FCSTD DOCUMENT  (FreeCAD 1.0R)
Label: mpair
License: All rights reserved
LicenseURL: https://en.wikipedia.org/wiki/All_rights_reserved
objects: Part::Feature×225, App::Link×145, App::Part×35, PartDesign::CoordinateSystem×1, Sketcher::SketchObject×1
note: 228 computed .brp shape members not serialized (recipe doc carries the construction recipe); baked Part::Feature solids carry a one-line shape summary decoded from their .brp

FEATURE [PartDesign::CoordinateSystem] Local_CS_39ef
  AttacherType = Attacher::AttachEngine3D
  MapMode = 2
FEATURE [Part::Feature] Pcb_39ef
  shape: bbox 100 x 102 x 1.6 mm, 117 faces (baked)
FEATURE [Sketcher::SketchObject] PCB_Sketch_39ef
  ArcFitTolerance = 1e-06
  FullyConstrained = false
  MakeInternals = false
  sketch-geometry (4):
    g0: LineSegment StartX=20 StartY=-18 StartZ=0 EndX=120 EndY=-18 EndZ=0
    g1: LineSegment StartX=120 StartY=-18 StartZ=0 EndX=120 EndY=-120 EndZ=0
    g2: LineSegment StartX=120 StartY=-120 StartZ=0 EndX=20 EndY=-120 EndZ=0
    g3: LineSegment StartX=20 StartY=-120 StartZ=0 EndX=20 EndY=-18 EndZ=0
  constraints (4):
    c: Coincident(g2,g3)
    c: Coincident(g0,g3)
    c: Coincident(g1,g2)
    c: Coincident(g0,g1)
FEATURE [App::Part] Board_Geoms_39ef
  Group = -> [Pcb_39ef,PCB_Sketch_39ef]
  Origin = -> Origin
FEATURE [Part::Feature] Shape  label="R46_R_0603_1608Metric_774aaaae9ccb"
  Placement = pos=(48.7,-50.2,0) rot=(0,0,1;0rad)
  shape: bbox 1.6 x 0.8 x 0.45 mm, 26 faces (baked)
FEATURE [App::Link] R46_R_0603_1608Metric_774aaaae9ccb_ln_  label="R34_R_0603_1608Metric_f5142b1c6ad6"
  LinkPlacement = pos=(51.175,-36.55,0) rot=(0,0,1;1.5708rad)
  LinkedObject = -> Shape
  Placement = pos=(51.175,-36.55,0) rot=(0,0,1;1.5708rad)
FEATURE [Part::Feature] Shape001  label="L4_L_0805_2012Metric_8a03def62cda"
  Placement = pos=(36.31,-53.75,0) rot=(0,0,1;1.5708rad)
  shape: bbox 1.25 x 2 x 1.25 mm, 28 faces (baked)
FEATURE [Part::Feature] Shape002  label="C15_C_0603_1608Metric_07e9d6ced425"
  Placement = pos=(52.4,-28.375,0) rot=(0,0,1;1.5708rad)
  shape: bbox 0.8 x 1.6 x 0.8 mm, 28 faces (baked)
FEATURE [App::Link] R46_R_0603_1608Metric_774aaaae9ccb_ln_001  label="R17_R_0603_1608Metric_bdc7fd87b56f"
  LinkPlacement = pos=(47.1,-28.725,0) rot=(0,0,-1;1.5708rad)
  LinkedObject = -> Shape
  Placement = pos=(47.1,-28.725,0) rot=(0,0,-1;1.5708rad)
FEATURE [Part::Feature] Shape003  label="C27_CP_Elec_8x62_1d99a2359d83"
  Placement = pos=(42.6675,-54.45,0) rot=(0,0,1;0rad)
  shape: bbox 10.73 x 10.92 x 6.2 mm, 41 faces (baked)
FEATURE [App::Link] C15_C_0603_1608Metric_07e9d6ced425_ln_  label="C39_C_0603_1608Metric_8ad4aeb55371"
  LinkPlacement = pos=(41.4,-88.125,0) rot=(0,0,-1;1.5708rad)
  LinkedObject = -> Shape002
  Placement = pos=(41.4,-88.125,0) rot=(0,0,-1;1.5708rad)
FEATURE [Part::Feature] Shape004  label="L7_L_0603_1608Metric_04b4d3cc0712"
  Placement = pos=(66.8125,-31.6,0) rot=(0,0,1;0rad)
  shape: bbox 1.6 x 0.8 x 0.8 mm, 28 faces (baked)
FEATURE [Part::Feature] Part__Feature  label="DR74-2R2-R"
  shape: bbox 7.6 x 0.8 x 5.493 mm, 71 faces (baked)
FEATURE [Part::Feature] Part__Feature001  label="DR74-2R2-R001"
  shape: bbox 7.6 x 3.95 x 7.6 mm, 70 faces (baked)
FEATURE [App::Part] DR74_2R2_R  label="L13_DR74-2R2-R002_60edd9ad2b36"
  Group = -> [Part__Feature,Part__Feature001]
  Origin = -> Origin008
  Placement = pos=(81.1972,-77.9,0) rot=(1,0,0;1.5708rad)
FEATURE [App::Link] R46_R_0603_1608Metric_774aaaae9ccb_ln_002  label="R21_R_0603_1608Metric_3d0d8529494c"
  LinkPlacement = pos=(50.7,-28.425,0) rot=(0,0,-1;1.5708rad)
  LinkedObject = -> Shape
  Placement = pos=(50.7,-28.425,0) rot=(0,0,-1;1.5708rad)
FEATURE [App::Link] R46_R_0603_1608Metric_774aaaae9ccb_ln_003  label="R54_R_0603_1608Metric_98e4eba829c8"
  LinkPlacement = pos=(41.4,-91.5,0) rot=(0,0,-1;1.5708rad)
  LinkedObject = -> Shape
  Placement = pos=(41.4,-91.5,0) rot=(0,0,-1;1.5708rad)
FEATURE [Part::Feature] Shape005  label="U8_SOT_23_6_8216086f4dbc"
  Placement = pos=(78.15,-100.65,0) rot=(0,0,-1;1.5708rad)
  shape: bbox 2.9 x 2.8 x 1.55 mm, 124 faces (baked)
FEATURE [Part::Feature] Part__Feature002  label="BxB-ZR-SM4_6"
  Placement = pos=(-4.5,4e-16,-1.85) rot=(0,1,0;3.14159rad)
  shape: bbox 12 x 5 x 3.7 mm, 62 faces (baked)
FEATURE [Part::Feature] Part__Feature003  label="BxB-ZR-SM4 pins_6"
  Placement = pos=(-4.5,4e-16,-1.85) rot=(0,1,0;3.14159rad)
  shape: bbox 0.6 x 3.75 x 2.5 mm, 16 faces (baked)
FEATURE [Part::Feature] Part__Feature004  label="BxB-ZR-SM4 pins_007"
  Placement = pos=(-4.5,4e-16,-1.85) rot=(0,1,0;3.14159rad)
  shape: bbox 0.5 x 0.5 x 1.5 mm, 6 faces (baked)
FEATURE [Part::Feature] Part__Feature005  label="BxB-ZR-SM4 pins_008"
  Placement = pos=(-4.5,4e-16,-1.85) rot=(0,1,0;3.14159rad)
  shape: bbox 0.5 x 2.4 x 0.5 mm, 6 faces (baked)
FEATURE [Part::Feature] Part__Feature006  label="BxB-ZR-SM4 pins_009"
  Placement = pos=(-4.5,4e-16,-1.85) rot=(0,1,0;3.14159rad)
  shape: bbox 0.6 x 3.75 x 2.5 mm, 16 faces (baked)
FEATURE [Part::Feature] Part__Feature007  label="BxB-ZR-SM4 pins_010"
  Placement = pos=(-4.5,4e-16,-1.85) rot=(0,1,0;3.14159rad)
  shape: bbox 0.5 x 0.5 x 1.5 mm, 6 faces (baked)
FEATURE [Part::Feature] Part__Feature008  label="BxB-ZR-SM4 pins_011"
  Placement = pos=(-4.5,4e-16,-1.85) rot=(0,1,0;3.14159rad)
  shape: bbox 0.5 x 2.4 x 0.5 mm, 6 faces (baked)
FEATURE [Part::Feature] Part__Feature009  label="BxB-ZR-SM4 pins_012"
  Placement = pos=(-4.5,4e-16,-1.85) rot=(0,1,0;3.14159rad)
  shape: bbox 0.5 x 0.5 x 1.5 mm, 6 faces (baked)
FEATURE [Part::Feature] Part__Feature010  label="BxB-ZR-SM4 pins_013"
  Placement = pos=(-4.5,4e-16,-1.85) rot=(0,1,0;3.14159rad)
  shape: bbox 0.5 x 2.4 x 0.5 mm, 6 faces (baked)
FEATURE [Part::Feature] Part__Feature011  label="BxB-ZR-SM4 pins_014"
  Placement = pos=(-4.5,4e-16,-1.85) rot=(0,1,0;3.14159rad)
  shape: bbox 0.5 x 0.5 x 1.5 mm, 6 faces (baked)
FEATURE [Part::Feature] Part__Feature012  label="BxB-ZR-SM4 pins_015"
  Placement = pos=(-4.5,4e-16,-1.85) rot=(0,1,0;3.14159rad)
  shape: bbox 0.5 x 0.5 x 1.5 mm, 6 faces (baked)
FEATURE [Part::Feature] Part__Feature013  label="BxB-ZR-SM4 pins_016"
  Placement = pos=(-4.5,4e-16,-1.85) rot=(0,1,0;3.14159rad)
  shape: bbox 0.5 x 0.5 x 1.5 mm, 6 faces (baked)
FEATURE [Part::Feature] Part__Feature014  label="BxB-ZR-SM4 pins_017"
  Placement = pos=(-4.5,4e-16,-1.85) rot=(0,1,0;3.14159rad)
  shape: bbox 0.5 x 2.4 x 0.5 mm, 6 faces (baked)
FEATURE [Part::Feature] Part__Feature015  label="BxB-ZR-SM4 pins_018"
  Placement = pos=(-4.5,4e-16,-1.85) rot=(0,1,0;3.14159rad)
  shape: bbox 0.5 x 2.4 x 0.5 mm, 6 faces (baked)
FEATURE [Part::Feature] Part__Feature016  label="BxB-ZR-SM4 pins_019"
  Placement = pos=(-4.5,4e-16,-1.85) rot=(0,1,0;3.14159rad)
  shape: bbox 0.5 x 2.4 x 0.5 mm, 6 faces (baked)
FEATURE [App::Part] BxB_ZR_SM4_pins_6  label="BxB-ZR-SM4 pins_020"
  Group = -> [Part__Feature003,Part__Feature004,Part__Feature005,Part__Feature006,Part__Feature007,Part__Feature008,Part__Feature009,Part__Feature010,Part__Feature011,Part__Feature012,Part__Feature013,Part__Feature014,Part__Feature015,Part__Feature016]
  Origin = -> Origin009
FEATURE [App::Part] B6B_ZR_SM4_TF  label="J5_B6B-ZR-SM4-TF_bfa23934778d"
  Group = -> [Part__Feature002,BxB_ZR_SM4_pins_6]
  Origin = -> Origin010
  Placement = pos=(91.3,-112.4,0) rot=(0.57735,0.57735,0.57735;2.0944rad)
FEATURE [Part::Feature] Shape006  label="J9_Molex_AE_6410_03A_8847f52549e1"
  Placement = pos=(100.1,-117.7,0) rot=(0,0,1;1.5708rad)
  shape: bbox 5.8 x 7.62 x 15.26 mm, 91 faces (baked)
FEATURE [App::Link] R46_R_0603_1608Metric_774aaaae9ccb_ln_004  label="R7_R_0603_1608Metric_40a0c56f9955"
  LinkPlacement = pos=(103.65,-104.875,0) rot=(0,0,1;0rad)
  LinkedObject = -> Shape
  Placement = pos=(103.65,-104.875,0) rot=(0,0,1;0rad)
FEATURE [Part::Feature] Part__Feature017  label="part"
  shape: bbox 0.2197 x 0.2197 x 0.002 mm, 3 faces (baked)
FEATURE [Part::Feature] Part__Feature018  label="part001"
  shape: bbox 4.399 x 2.695 x 2.39 mm, 14 faces (baked)
FEATURE [Part::Feature] Part__Feature019  label="part002"
  shape: bbox 1.45 x 0.5096 x 1.323 mm, 14 faces (baked)
FEATURE [Part::Feature] Part__Feature020  label="part003"
  shape: bbox 1.45 x 0.5096 x 1.323 mm, 14 faces (baked)
FEATURE [Part::Feature] Part__Feature021  label="part004"
  shape: bbox 1.45 x 0.5096 x 1.323 mm, 14 faces (baked)
FEATURE [Part::Feature] Part__Feature022  label="part005"
  shape: bbox 1.45 x 0.5096 x 1.323 mm, 14 faces (baked)
FEATURE [App::Part] part  label="U6_part006_fb86ca2d76d7"
  Group = -> [Part__Feature017,Part__Feature018,Part__Feature019,Part__Feature020,Part__Feature021,Part__Feature022]
  Origin = -> Origin011
  Placement = pos=(40.2,-78.3,0) rot=(0,0,1;1.5708rad)
FEATURE [Part::Feature] Shape007  label="C34_C_1812_4532Metric_c9e1e99fbcf3"
  Placement = pos=(44.2,-78.3,0) rot=(0,0,-1;1.5708rad)
  shape: bbox 3.2 x 4.5 x 2.5 mm, 28 faces (baked)
FEATURE [App::Link] R46_R_0603_1608Metric_774aaaae9ccb_ln_005  label="R13_R_0603_1608Metric_f67d6ac71e9b"
  LinkPlacement = pos=(47.5,-24.5,0) rot=(0,0,-1;1.5708rad)
  LinkedObject = -> Shape
  Placement = pos=(47.5,-24.5,0) rot=(0,0,-1;1.5708rad)
FEATURE [App::Link] R46_R_0603_1608Metric_774aaaae9ccb_ln_006  label="R12_R_0603_1608Metric_d3075d49b59f"
  LinkPlacement = pos=(28.225,-19.95,0) rot=(0,0,1;0rad)
  LinkedObject = -> Shape
  Placement = pos=(28.225,-19.95,0) rot=(0,0,1;0rad)
FEATURE [Part::Feature] Shape008  label="C42_CP_Elec_8x10_2bb510fd45c5"
  Placement = pos=(73.1,-112.4,0) rot=(0,0,-1;1.5708rad)
  shape: bbox 10.92 x 10.73 x 10 mm, 41 faces (baked)
FEATURE [App::Link] R46_R_0603_1608Metric_774aaaae9ccb_ln_007  label="R3_R_0603_1608Metric_7ba40911dab3"
  LinkPlacement = pos=(110.45,-103.7,0) rot=(0,0,-1;1.5708rad)
  LinkedObject = -> Shape
  Placement = pos=(110.45,-103.7,0) rot=(0,0,-1;1.5708rad)
FEATURE [App::Link] R46_R_0603_1608Metric_774aaaae9ccb_ln_008  label="R64_R_0603_1608Metric_9be8635e4ac9"
  LinkPlacement = pos=(111.6,-63.5,0) rot=(0,0,-1;1.5708rad)
  LinkedObject = -> Shape
  Placement = pos=(111.6,-63.5,0) rot=(0,0,-1;1.5708rad)
FEATURE [Part::Feature] Part__Feature023  label="BarrelJack_CUI_PJ-063AH_Horizontal"
  shape: bbox 9.8 x 8.6 x 11.9 mm, 54 faces (baked)
FEATURE [Part::Feature] Part__Feature024  label="BarrelJack_CUI_PJ-063AH_Horizontal001"
  shape: bbox 10 x 13 x 12 mm, 42 faces (baked)
FEATURE [App::Part] BarrelJack_CUI_PJ_063AH_Horizontal  label="J1_BarrelJack_CUI_PJ-063AH_Horizontal002_36d1827e98da"
  Group = -> [Part__Feature023,Part__Feature024]
  Origin = -> Origin012
  Placement = pos=(32.4,-112.4,0) rot=(0,0,-1;1.5708rad)
FEATURE [Part::Feature] Shape009  label="Q8_SC_59_2bd4244db7e1"
  Placement = pos=(114.8,-108.75,0) rot=(0,0,1;3.14159rad)
  shape: bbox 2.8 x 3 x 1.3 mm, 76 faces (baked)
FEATURE [Part::Feature] Shape010  label="C25_C_0805_2012Metric_74a1367a9602"
  Placement = pos=(58.2,-56.55,0) rot=(0,0,1;1.5708rad)
  shape: bbox 1.25 x 2 x 1.25 mm, 28 faces (baked)
FEATURE [App::Link] R46_R_0603_1608Metric_774aaaae9ccb_ln_009  label="R70_R_0603_1608Metric_297dd1acad90"
  LinkPlacement = pos=(81.7,-64.1,0) rot=(0,0,-1;1.5708rad)
  LinkedObject = -> Shape
  Placement = pos=(81.7,-64.1,0) rot=(0,0,-1;1.5708rad)
FEATURE [App::Link] C15_C_0603_1608Metric_07e9d6ced425_ln_001  label="C23_C_0603_1608Metric_376995170c63"
  LinkPlacement = pos=(69.925,-31.6,0) rot=(0,0,1;0rad)
  LinkedObject = -> Shape002
  Placement = pos=(69.925,-31.6,0) rot=(0,0,1;0rad)
FEATURE [App::Link] L4_L_0805_2012Metric_8a03def62cda_ln_  label="L5_L_0805_2012Metric_fc17c2d6df8f"
  LinkPlacement = pos=(98.65,-103.838,0) rot=(0,0,-1;1.5708rad)
  LinkedObject = -> Shape001
  Placement = pos=(98.65,-103.838,0) rot=(0,0,-1;1.5708rad)
FEATURE [App::Link] C15_C_0603_1608Metric_07e9d6ced425_ln_002  label="C29_C_0603_1608Metric_f624abb60192"
  LinkPlacement = pos=(52,-53.8,0) rot=(0,0,1;0rad)
  LinkedObject = -> Shape002
  Placement = pos=(52,-53.8,0) rot=(0,0,1;0rad)
FEATURE [Part::Feature] Shape011  label="R51_R_0805_2012Metric_3a37762b02a9"
  Placement = pos=(66.95,-97.15,0) rot=(0,0,-1;1.5708rad)
  shape: bbox 1.2 x 2 x 0.45 mm, 26 faces (baked)
FEATURE [App::Link] C15_C_0603_1608Metric_07e9d6ced425_ln_003  label="C5_C_0603_1608Metric_a1c9e7e04d42"
  LinkPlacement = pos=(36.31,-48.75,0) rot=(0,0,-1;1.5708rad)
  LinkedObject = -> Shape002
  Placement = pos=(36.31,-48.75,0) rot=(0,0,-1;1.5708rad)
FEATURE [App::Link] R46_R_0603_1608Metric_774aaaae9ccb_ln_010  label="R53_R_0603_1608Metric_e281e5424af1"
  LinkPlacement = pos=(39.5,-88.1,0) rot=(0,0,1;1.5708rad)
  LinkedObject = -> Shape
  Placement = pos=(39.5,-88.1,0) rot=(0,0,1;1.5708rad)
FEATURE [App::Link] R46_R_0603_1608Metric_774aaaae9ccb_ln_011  label="R60_R_0603_1608Metric_86f9834c2b51"
  LinkPlacement = pos=(115.4,-63.5,0) rot=(0,0,-1;1.5708rad)
  LinkedObject = -> Shape
  Placement = pos=(115.4,-63.5,0) rot=(0,0,-1;1.5708rad)
FEATURE [Part::Feature] Shape012  label="D6_D_SMB_3d57ee7d56c4"
  Placement = pos=(60.2,-43.3,0) rot=(0,0,-1;1.5708rad)
  shape: bbox 3.55 x 5.3 x 2.15 mm, 41 faces (baked)
FEATURE [App::Link] Q8_SC_59_2bd4244db7e1_ln_  label="D14_SC_59_adce9ebe72b1"
  LinkPlacement = pos=(62.75,-97.15,0) rot=(0,0,1;0rad)
  LinkedObject = -> Shape009
  Placement = pos=(62.75,-97.15,0) rot=(0,0,1;0rad)
FEATURE [App::Link] C15_C_0603_1608Metric_07e9d6ced425_ln_004  label="C49_C_0603_1608Metric_8a9601e40898"
  LinkPlacement = pos=(81.9,-84.4,0) rot=(0,0,-1;1.5708rad)
  LinkedObject = -> Shape002
  Placement = pos=(81.9,-84.4,0) rot=(0,0,-1;1.5708rad)
FEATURE [App::Link] Q8_SC_59_2bd4244db7e1_ln_001  label="D10_SC_59_9d504f3714de"
  LinkPlacement = pos=(57.1,-97.15,0) rot=(0,0,1;3.14159rad)
  LinkedObject = -> Shape009
  Placement = pos=(57.1,-97.15,0) rot=(0,0,1;3.14159rad)
FEATURE [Part::Feature] Shape013  label="D3_D_0603_7257a63e26b1"
  Placement = pos=(54.2,-23.2625,0) rot=(0,0,-1;1.5708rad)
  shape: bbox 0.87 x 1.6 x 0.66 mm, 39 faces (baked)
FEATURE [Part::Feature] Shape014  label="C7_C_1210_3225Metric_ef0ee58cb2a3"
  Placement = pos=(99.45,-97.075,0) rot=(0,0,1;1.5708rad)
  shape: bbox 2.5 x 3.2 x 2.5 mm, 28 faces (baked)
FEATURE [Part::Feature] Shape015  label="D16_D_SOD_123_001db0ef50de"
  Placement = pos=(108.8,-107.1,0) rot=(0,0,1;0rad)
  shape: bbox 3.8 x 1.6 x 1.25 mm, 67 faces (baked)
FEATURE [Part::Feature] Part__Feature025  label="part006"
  shape: bbox 0.1295 x 0.1295 x 0.003 mm, 3 faces (baked)
FEATURE [Part::Feature] Part__Feature026  label="part007"
  shape: bbox 2.59 x 3.404 x 2.133 mm, 6 faces (baked)
FEATURE [Part::Feature] Part__Feature027  label="part008"
  shape: bbox 0.829 x 0.533 x 0.381 mm, 8 faces (baked)
FEATURE [Part::Feature] Part__Feature028  label="part009"
  shape: bbox 0.829 x 0.533 x 0.381 mm, 8 faces (baked)
FEATURE [Part::Feature] Part__Feature029  label="part010"
  shape: bbox 0.829 x 0.533 x 0.381 mm, 8 faces (baked)
FEATURE [Part::Feature] Part__Feature030  label="part011"
  shape: bbox 0.829 x 0.533 x 0.381 mm, 8 faces (baked)
FEATURE [App::Part] part001  label="L8_part012_f921aaf74477"
  Group = -> [Part__Feature025,Part__Feature026,Part__Feature027,Part__Feature028,Part__Feature029,Part__Feature030]
  Origin = -> Origin013
  Placement = pos=(45.627,-36.5,0) rot=(0,0,1;1.5708rad)
FEATURE [Part::Feature] Shape016  label="RN1_R_Array_Concave_4x0603_af55f0de138e"
  Placement = pos=(51.55,-24.85,0) rot=(0,0,1;0rad)
  shape: bbox 1.6 x 3.2 x 0.6 mm, 140 faces (baked)
FEATURE [App::Link] C7_C_1210_3225Metric_ef0ee58cb2a3_ln_  label="C41_C_1210_3225Metric_231fadff6d53"
  LinkPlacement = pos=(66.6,-109.15,0) rot=(0,0,1;1.5708rad)
  LinkedObject = -> Shape014
  Placement = pos=(66.6,-109.15,0) rot=(0,0,1;1.5708rad)
FEATURE [Part::Feature] Part__Feature031  label="part012"
  shape: bbox 0.2299 x 0.2299 x 0.003 mm, 3 faces (baked)
FEATURE [Part::Feature] Part__Feature032  label="part013"
  shape: bbox 4.602 x 3.915 x 3 mm, 14 faces (baked)
FEATURE [Part::Feature] Part__Feature033  label="part014"
  shape: bbox 1.296 x 0.5094 x 1.627 mm, 14 faces (baked)
FEATURE [Part::Feature] Part__Feature034  label="part015"
  shape: bbox 1.296 x 0.5094 x 1.627 mm, 14 faces (baked)
FEATURE [Part::Feature] Part__Feature035  label="part016"
  shape: bbox 1.296 x 0.5094 x 1.627 mm, 14 faces (baked)
FEATURE [Part::Feature] Part__Feature036  label="part017"
  shape: bbox 1.296 x 0.5094 x 1.627 mm, 14 faces (baked)
FEATURE [App::Part] part002  label="U7_part018_2105863d2e2c"
  Group = -> [Part__Feature031,Part__Feature032,Part__Feature033,Part__Feature034,Part__Feature035,Part__Feature036]
  Origin = -> Origin014
  Placement = pos=(74.5,-70.3,0) rot=(0,0,1;0rad)
FEATURE [Part::Feature] Shape017  label="C26_C_1206_3216Metric_2a08b5551de6"
  Placement = pos=(57.5,-65.025,0) rot=(0,0,1;1.5708rad)
  shape: bbox 1.6 x 3.2 x 1.6 mm, 28 faces (baked)
FEATURE [App::Link] R46_R_0603_1608Metric_774aaaae9ccb_ln_012  label="R37_R_0603_1608Metric_6502443f79bd"
  LinkPlacement = pos=(60.65,-36.55,0) rot=(0,0,1;1.5708rad)
  LinkedObject = -> Shape
  Placement = pos=(60.65,-36.55,0) rot=(0,0,1;1.5708rad)
FEATURE [App::Link] C15_C_0603_1608Metric_07e9d6ced425_ln_005  label="C4_C_0603_1608Metric_b8aa947e1a63"
  LinkPlacement = pos=(36.2,-112.4,0) rot=(0,0,-1;1.5708rad)
  LinkedObject = -> Shape002
  Placement = pos=(36.2,-112.4,0) rot=(0,0,-1;1.5708rad)
FEATURE [App::Link] C7_C_1210_3225Metric_ef0ee58cb2a3_ln_001  label="C40_C_1210_3225Metric_2fc55fe14432"
  LinkPlacement = pos=(66.6,-115.675,0) rot=(0,0,-1;1.5708rad)
  LinkedObject = -> Shape014
  Placement = pos=(66.6,-115.675,0) rot=(0,0,-1;1.5708rad)
FEATURE [App::Link] R46_R_0603_1608Metric_774aaaae9ccb_ln_013  label="R61_R_0603_1608Metric_1d752b88a0c3"
  LinkPlacement = pos=(107.8,-63.5,0) rot=(0,0,-1;1.5708rad)
  LinkedObject = -> Shape
  Placement = pos=(107.8,-63.5,0) rot=(0,0,-1;1.5708rad)
FEATURE [Part::Feature] Shape018  label="D1_D_SMA_e719b518da9d"
  Placement = pos=(40.36,-45.45,0) rot=(0,0,-1;1.5708rad)
  shape: bbox 2.7 x 5 x 2.22 mm, 41 faces (baked)
FEATURE [App::Link] R46_R_0603_1608Metric_774aaaae9ccb_ln_014  label="R20_R_0603_1608Metric_5ae41c8f7d63"
  LinkPlacement = pos=(44.675,-20.35,0) rot=(0,0,1;0rad)
  LinkedObject = -> Shape
  Placement = pos=(44.675,-20.35,0) rot=(0,0,1;0rad)
FEATURE [Part::Feature] Part__Feature037  label="SRR1208"
  shape: bbox 12.7 x 2.2 x 12.7 mm, 30 faces (baked)
FEATURE [Part::Feature] Part__Feature038  label="SRR1209"
  shape: bbox 12.7 x 7.2 x 12.7 mm, 40 faces (baked)
FEATURE [App::Part] SRR1208  label="L11_SRR1210_1625587d1eb0"
  Group = -> [Part__Feature037,Part__Feature038]
  Origin = -> Origin015
  Placement = pos=(48.4,-112.25,0.2) rot=(1,0,0;1.5708rad)
FEATURE [App::Link] L4_L_0805_2012Metric_8a03def62cda_ln_001  label="L2_L_0805_2012Metric_cfc35715fd5a"
  LinkPlacement = pos=(36.2,-117.4,0) rot=(0,0,1;1.5708rad)
  LinkedObject = -> Shape001
  Placement = pos=(36.2,-117.4,0) rot=(0,0,1;1.5708rad)
FEATURE [App::Link] C15_C_0603_1608Metric_07e9d6ced425_ln_006  label="C17_C_0603_1608Metric_233d63a9970e"
  LinkPlacement = pos=(60.6625,-33.375,0) rot=(0,0,1;1.5708rad)
  LinkedObject = -> Shape002
  Placement = pos=(60.6625,-33.375,0) rot=(0,0,1;1.5708rad)
FEATURE [App::Link] D16_D_SOD_123_001db0ef50de_ln_  label="D13_D_SOD_123_f0bbc3cf7802"
  LinkPlacement = pos=(48.8,-94.6,0) rot=(0,0,1;1.5708rad)
  LinkedObject = -> Shape015
  Placement = pos=(48.8,-94.6,0) rot=(0,0,1;1.5708rad)
FEATURE [App::Link] C15_C_0603_1608Metric_07e9d6ced425_ln_007  label="C8_C_0603_1608Metric_3d25220c7f24"
  LinkPlacement = pos=(100.55,-104.1,0) rot=(0,0,1;1.5708rad)
  LinkedObject = -> Shape002
  Placement = pos=(100.55,-104.1,0) rot=(0,0,1;1.5708rad)
FEATURE [App::Link] R46_R_0603_1608Metric_774aaaae9ccb_ln_015  label="R14_R_0603_1608Metric_b8c0ad13ef43"
  LinkPlacement = pos=(43.7,-24.475,0) rot=(0,0,-1;1.5708rad)
  LinkedObject = -> Shape
  Placement = pos=(43.7,-24.475,0) rot=(0,0,-1;1.5708rad)
FEATURE [App::Link] U8_SOT_23_6_8216086f4dbc_ln_  label="U9_SOT_23_6_7fa43c93b1dc"
  LinkPlacement = pos=(78.15,-85.1625,0) rot=(0,0,-1;1.5708rad)
  LinkedObject = -> Shape005
  Placement = pos=(78.15,-85.1625,0) rot=(0,0,-1;1.5708rad)
FEATURE [App::Link] C7_C_1210_3225Metric_ef0ee58cb2a3_ln_002  label="C44_C_1210_3225Metric_7e9aa11df215"
  LinkPlacement = pos=(74.2,-95.2,0) rot=(0,0,-1;1.5708rad)
  LinkedObject = -> Shape014
  Placement = pos=(74.2,-95.2,0) rot=(0,0,-1;1.5708rad)
FEATURE [App::Link] R46_R_0603_1608Metric_774aaaae9ccb_ln_016  label="R56_R_0603_1608Metric_0e1817b85848"
  LinkPlacement = pos=(79.625,-103.6,0) rot=(0,0,1;3.14159rad)
  LinkedObject = -> Shape
  Placement = pos=(79.625,-103.6,0) rot=(0,0,1;3.14159rad)
FEATURE [App::Link] Q8_SC_59_2bd4244db7e1_ln_002  label="D11_SC_59_5ee113a929a4"
  LinkPlacement = pos=(46.8,-84.6,0) rot=(0,0,1;0rad)
  LinkedObject = -> Shape009
  Placement = pos=(46.8,-84.6,0) rot=(0,0,1;0rad)
FEATURE [App::Link] C25_C_0805_2012Metric_74a1367a9602_ln_  label="C36_C_0805_2012Metric_0ec6a73c6179"
  LinkPlacement = pos=(43.6,-84.6,0) rot=(0,0,1;1.5708rad)
  LinkedObject = -> Shape010
  Placement = pos=(43.6,-84.6,0) rot=(0,0,1;1.5708rad)
FEATURE [App::Link] Q8_SC_59_2bd4244db7e1_ln_003  label="D12_SC_59_1be8da5ed14b"
  LinkPlacement = pos=(46.4,-88.8,0) rot=(0,0,1;0rad)
  LinkedObject = -> Shape009
  Placement = pos=(46.4,-88.8,0) rot=(0,0,1;0rad)
FEATURE [App::Link] C15_C_0603_1608Metric_07e9d6ced425_ln_008  label="C37_C_0603_1608Metric_7e360995dad7"
  LinkPlacement = pos=(43.3,-88.1,0) rot=(0,0,-1;1.5708rad)
  LinkedObject = -> Shape002
  Placement = pos=(43.3,-88.1,0) rot=(0,0,-1;1.5708rad)
FEATURE [App::Link] C15_C_0603_1608Metric_07e9d6ced425_ln_009  label="C22_C_0603_1608Metric_4ce7b6444197"
  LinkPlacement = pos=(55.8,-20.9,0) rot=(0,0,-1;1.5708rad)
  LinkedObject = -> Shape002
  Placement = pos=(55.8,-20.9,0) rot=(0,0,-1;1.5708rad)
FEATURE [App::Link] C15_C_0603_1608Metric_07e9d6ced425_ln_010  label="C10_C_0603_1608Metric_b3e33615cffe"
  LinkPlacement = pos=(48.9,-28.675,0) rot=(0,0,1;1.5708rad)
  LinkedObject = -> Shape002
  Placement = pos=(48.9,-28.675,0) rot=(0,0,1;1.5708rad)
FEATURE [Part::Feature] Shape019  label="Q1_SOT_363_SC_70_6_98748a45afd2"
  Placement = pos=(104.9,-96.225,0) rot=(0,0,1;3.14159rad)
  shape: bbox 2 x 2 x 1.05 mm, 118 faces (baked)
FEATURE [App::Link] R46_R_0603_1608Metric_774aaaae9ccb_ln_017  label="R43_R_0603_1608Metric_f50d1f320f3e"
  LinkPlacement = pos=(52,-55.6,0) rot=(0,0,1;0rad)
  LinkedObject = -> Shape
  Placement = pos=(52,-55.6,0) rot=(0,0,1;0rad)
FEATURE [App::Link] L13_DR74_2R2_R002_60edd9ad2b36_ln_  label="L12_DR74-2R2-R002_3baf6c89d8cf"
  LinkPlacement = pos=(81.2,-93.4,0) rot=(1,0,0;1.5708rad)
  LinkedObject = -> DR74_2R2_R
  Placement = pos=(81.2,-93.4,0) rot=(1,0,0;1.5708rad)
FEATURE [App::Link] Q8_SC_59_2bd4244db7e1_ln_004  label="D7_SC_59_690d85af358d"
  LinkPlacement = pos=(58.2,-60.375,0) rot=(0,0,1;0rad)
  LinkedObject = -> Shape009
  Placement = pos=(58.2,-60.375,0) rot=(0,0,1;0rad)
FEATURE [App::Link] R46_R_0603_1608Metric_774aaaae9ccb_ln_018  label="R58_R_0603_1608Metric_e315c32501a6"
  LinkPlacement = pos=(79.625,-88.1,0) rot=(0,0,1;3.14159rad)
  LinkedObject = -> Shape
  Placement = pos=(79.625,-88.1,0) rot=(0,0,1;3.14159rad)
FEATURE [App::Link] R46_R_0603_1608Metric_774aaaae9ccb_ln_019  label="R67_R_0603_1608Metric_de1c96668fdd"
  LinkPlacement = pos=(95.875,-75.7,0) rot=(0,0,1;0rad)
  LinkedObject = -> Shape
  Placement = pos=(95.875,-75.7,0) rot=(0,0,1;0rad)
FEATURE [App::Link] D3_D_0603_7257a63e26b1_ln_  label="D4_D_0603_679e1ba17305"
  LinkPlacement = pos=(54.2,-26.4375,0) rot=(0,0,1;1.5708rad)
  LinkedObject = -> Shape013
  Placement = pos=(54.2,-26.4375,0) rot=(0,0,1;1.5708rad)
FEATURE [Part::Feature] Part__Feature039  label="BxB-ZR-SM4_5"
  Placement = pos=(-5.25,4e-16,-1.85) rot=(0,1,0;3.14159rad)
  shape: bbox 10.5 x 5 x 3.7 mm, 62 faces (baked)
FEATURE [Part::Feature] Part__Feature040  label="BxB-ZR-SM4 pins_5"
  Placement = pos=(-5.25,4e-16,-1.85) rot=(0,1,0;3.14159rad)
  shape: bbox 0.6 x 3.75 x 2.5 mm, 16 faces (baked)
FEATURE [Part::Feature] Part__Feature041  label="BxB-ZR-SM4 pins_021"
  Placement = pos=(-5.25,4e-16,-1.85) rot=(0,1,0;3.14159rad)
  shape: bbox 0.5 x 0.5 x 1.5 mm, 6 faces (baked)
FEATURE [Part::Feature] Part__Feature042  label="BxB-ZR-SM4 pins_022"
  Placement = pos=(-5.25,4e-16,-1.85) rot=(0,1,0;3.14159rad)
  shape: bbox 0.5 x 2.4 x 0.5 mm, 6 faces (baked)
FEATURE [Part::Feature] Part__Feature043  label="BxB-ZR-SM4 pins_023"
  Placement = pos=(-5.25,4e-16,-1.85) rot=(0,1,0;3.14159rad)
  shape: bbox 0.6 x 3.75 x 2.5 mm, 16 faces (baked)
FEATURE [Part::Feature] Part__Feature044  label="BxB-ZR-SM4 pins_024"
  Placement = pos=(-5.25,4e-16,-1.85) rot=(0,1,0;3.14159rad)
  shape: bbox 0.5 x 0.5 x 1.5 mm, 6 faces (baked)
FEATURE [Part::Feature] Part__Feature045  label="BxB-ZR-SM4 pins_025"
  Placement = pos=(-5.25,4e-16,-1.85) rot=(0,1,0;3.14159rad)
  shape: bbox 0.5 x 2.4 x 0.5 mm, 6 faces (baked)
FEATURE [Part::Feature] Part__Feature046  label="BxB-ZR-SM4 pins_026"
  Placement = pos=(-5.25,4e-16,-1.85) rot=(0,1,0;3.14159rad)
  shape: bbox 0.5 x 0.5 x 1.5 mm, 6 faces (baked)
FEATURE [Part::Feature] Part__Feature047  label="BxB-ZR-SM4 pins_027"
  Placement = pos=(-5.25,4e-16,-1.85) rot=(0,1,0;3.14159rad)
  shape: bbox 0.5 x 2.4 x 0.5 mm, 6 faces (baked)
FEATURE [Part::Feature] Part__Feature048  label="BxB-ZR-SM4 pins_028"
  Placement = pos=(-5.25,4e-16,-1.85) rot=(0,1,0;3.14159rad)
  shape: bbox 0.5 x 0.5 x 1.5 mm, 6 faces (baked)
FEATURE [Part::Feature] Part__Feature049  label="BxB-ZR-SM4 pins_029"
  Placement = pos=(-5.25,4e-16,-1.85) rot=(0,1,0;3.14159rad)
  shape: bbox 0.5 x 0.5 x 1.5 mm, 6 faces (baked)
FEATURE [Part::Feature] Part__Feature050  label="BxB-ZR-SM4 pins_030"
  Placement = pos=(-5.25,4e-16,-1.85) rot=(0,1,0;3.14159rad)
  shape: bbox 0.5 x 2.4 x 0.5 mm, 6 faces (baked)
FEATURE [Part::Feature] Part__Feature051  label="BxB-ZR-SM4 pins_031"
  Placement = pos=(-5.25,4e-16,-1.85) rot=(0,1,0;3.14159rad)
  shape: bbox 0.5 x 2.4 x 0.5 mm, 6 faces (baked)
FEATURE [App::Part] BxB_ZR_SM4_pins_5  label="BxB-ZR-SM4 pins_032"
  Group = -> [Part__Feature040,Part__Feature041,Part__Feature042,Part__Feature043,Part__Feature044,Part__Feature045,Part__Feature046,Part__Feature047,Part__Feature048,Part__Feature049,Part__Feature050,Part__Feature051]
  Origin = -> Origin016
FEATURE [App::Part] B5B_ZR_SM4_TF  label="J6_B5B-ZR-SM4-TF_078686d8772e"
  Group = -> [Part__Feature039,BxB_ZR_SM4_pins_5]
  Origin = -> Origin017
  Placement = pos=(98.2,-63.9,0) rot=(1,0,0;1.5708rad)
FEATURE [App::Link] R46_R_0603_1608Metric_774aaaae9ccb_ln_020  label="R44_R_0603_1608Metric_4ad3b6abe00a"
  LinkPlacement = pos=(49.4,-56.35,0) rot=(0,0,1;1.5708rad)
  LinkedObject = -> Shape
  Placement = pos=(49.4,-56.35,0) rot=(0,0,1;1.5708rad)
FEATURE [App::Link] C25_C_0805_2012Metric_74a1367a9602_ln_001  label="C24_C_0805_2012Metric_f408f941c3c0"
  LinkPlacement = pos=(49.15,-36.55,0) rot=(0,0,1;1.5708rad)
  LinkedObject = -> Shape010
  Placement = pos=(49.15,-36.55,0) rot=(0,0,1;1.5708rad)
FEATURE [App::Link] R46_R_0603_1608Metric_774aaaae9ccb_ln_021  label="R38_R_0603_1608Metric_163acdffd42d"
  LinkPlacement = pos=(62.575,-36.55,0) rot=(0,0,-1;1.5708rad)
  LinkedObject = -> Shape
  Placement = pos=(62.575,-36.55,0) rot=(0,0,-1;1.5708rad)
FEATURE [App::Link] C7_C_1210_3225Metric_ef0ee58cb2a3_ln_003  label="C53_C_1210_3225Metric_84c545a4b120"
  LinkPlacement = pos=(88.2,-84.9,0) rot=(0,0,-1;1.5708rad)
  LinkedObject = -> Shape014
  Placement = pos=(88.2,-84.9,0) rot=(0,0,-1;1.5708rad)
FEATURE [App::Link] R46_R_0603_1608Metric_774aaaae9ccb_ln_022  label="R9_R_0603_1608Metric_296df60f6211"
  LinkPlacement = pos=(107.95,-101.325,0) rot=(0,0,1;1.5708rad)
  LinkedObject = -> Shape
  Placement = pos=(107.95,-101.325,0) rot=(0,0,1;1.5708rad)
FEATURE [App::Link] D6_D_SMB_3d57ee7d56c4_ln_  label="D5_D_SMB_7e141658368b"
  LinkPlacement = pos=(45.6,-45.6,0) rot=(0,0,-1;1.5708rad)
  LinkedObject = -> Shape012
  Placement = pos=(45.6,-45.6,0) rot=(0,0,-1;1.5708rad)
FEATURE [Part::Feature] Part__Feature052  label="pines"
  Placement = pos=(0,0,0) rot=(1,0,0;1.5708rad)
  shape: bbox 9 x 1 x 0.8602 mm, 18 faces (baked)
FEATURE [Part::Feature] Part__Feature053  label="cuerpo"
  Placement = pos=(-3,-1.75,0) rot=(0,0,1;0rad)
  shape: bbox 6 x 3.5 x 1.8 mm, 43 faces (baked)
FEATURE [Part::Feature] Part__Feature054  label="boton"
  Placement = pos=(-0.9,-0.63,0) rot=(0,0,1;0rad)
  shape: bbox 1.8 x 1.25 x 2 mm, 18 faces (baked)
FEATURE [App::Part] ASSEMBLY  label="SW1_ASSEMBLY_b6ed21c688b7"
  Group = -> [Part__Feature052,Part__Feature053,Part__Feature054]
  Origin = -> Origin018
  Placement = pos=(110.79,-67.3,0) rot=(0,0,1;0rad)
FEATURE [Part::Feature] Shape020  label="T1_PA4065NL_3af35f8743a4"
  Placement = pos=(59.5,-78.275,-0.1) rot=(0,0,1;1.5708rad)
  shape: bbox 13.11 x 17.06 x 12.3 mm, 343 faces (baked)
FEATURE [App::Link] R46_R_0603_1608Metric_774aaaae9ccb_ln_023  label="R52_R_0603_1608Metric_9e8095a25d8f"
  LinkPlacement = pos=(43.3,-91.5,0) rot=(0,0,-1;1.5708rad)
  LinkedObject = -> Shape
  Placement = pos=(43.3,-91.5,0) rot=(0,0,-1;1.5708rad)
FEATURE [App::Link] J1_BarrelJack_CUI_PJ_063AH_Horizontal002_36d1827e98da_ln_  label="J2_BarrelJack_CUI_PJ-063AH_Horizontal002_65223e44f8ae"
  LinkPlacement = pos=(32.51,-48.75,0) rot=(0,0,-1;1.5708rad)
  LinkedObject = -> BarrelJack_CUI_PJ_063AH_Horizontal
  Placement = pos=(32.51,-48.75,0) rot=(0,0,-1;1.5708rad)
FEATURE [App::Link] R46_R_0603_1608Metric_774aaaae9ccb_ln_024  label="R57_R_0603_1608Metric_7448bebd62c0"
  LinkPlacement = pos=(76.4,-103.6,0) rot=(0,0,1;3.14159rad)
  LinkedObject = -> Shape
  Placement = pos=(76.4,-103.6,0) rot=(0,0,1;3.14159rad)
FEATURE [App::Link] D1_D_SMA_e719b518da9d_ln_  label="D2_D_SMA_857ed7a0b165"
  LinkPlacement = pos=(39.5,-110.45,0) rot=(0,0,1;1.5708rad)
  LinkedObject = -> Shape018
  Placement = pos=(39.5,-110.45,0) rot=(0,0,1;1.5708rad)
FEATURE [App::Link] C15_C_0603_1608Metric_07e9d6ced425_ln_011  label="C30_C_0603_1608Metric_dd2b13620af9"
  LinkPlacement = pos=(52,-52,0) rot=(0,0,1;0rad)
  LinkedObject = -> Shape002
  Placement = pos=(52,-52,0) rot=(0,0,1;0rad)
FEATURE [App::Link] C15_C_0603_1608Metric_07e9d6ced425_ln_012  label="C38_C_0603_1608Metric_454104598dfe"
  LinkPlacement = pos=(69.7,-103.9,0) rot=(0,0,1;0rad)
  LinkedObject = -> Shape002
  Placement = pos=(69.7,-103.9,0) rot=(0,0,1;0rad)
FEATURE [Part::Feature] Part__Feature055  label="adbeea57-9c39-11ed-93f0-dde97e994e83_part"
  shape: bbox 2.5 x 4.5 x 1.5 mm, 12 faces (baked)
FEATURE [App::Part] adbeea57_9c39_11ed_93f0_dde97e994e83  label="adbeea57-9c39-11ed-93f0-dde97e994e83"
  Group = -> [Part__Feature055]
  Origin = -> Origin019
FEATURE [Part::Feature] Part__Feature056  label="adbeea58-9c39-11ed-93f0-dde97e994e83_part"
  shape: bbox 2.5 x 1.6 x 0.4 mm, 12 faces (baked)
FEATURE [App::Part] adbeea58_9c39_11ed_93f0_dde97e994e83  label="adbeea58-9c39-11ed-93f0-dde97e994e83"
  Group = -> [Part__Feature056]
  Origin = -> Origin020
FEATURE [Part::Feature] Part__Feature057  label="adbeea59-9c39-11ed-93f0-dde97e994e83_part"
  shape: bbox 1.5 x 0.4 x 0.4 mm, 6 faces (baked)
FEATURE [Part::Feature] Part__Feature058  label="adbeea59-9c39-11ed-93f0-dde97e994e83_part001"
  shape: bbox 1.5 x 0.4 x 0.4 mm, 6 faces (baked)
FEATURE [Part::Feature] Part__Feature059  label="adbeea59-9c39-11ed-93f0-dde97e994e83_part002"
  shape: bbox 1.5 x 0.4 x 0.4 mm, 6 faces (baked)
FEATURE [App::Part] adbeea59_9c39_11ed_93f0_dde97e994e83_part  label="adbeea59-9c39-11ed-93f0-dde97e994e83_part003"
  Group = -> [Part__Feature057,Part__Feature058,Part__Feature059]
  Origin = -> Origin021
FEATURE [App::Part] adbeea59_9c39_11ed_93f0_dde97e994e83  label="adbeea59-9c39-11ed-93f0-dde97e994e83"
  Group = -> [adbeea59_9c39_11ed_93f0_dde97e994e83_part]
  Origin = -> Origin022
FEATURE [App::Part] adbeea56_9c39_11ed_93f0_dde97e994e83  label="adbeea56-9c39-11ed-93f0-dde97e994e83"
  Group = -> [adbeea57_9c39_11ed_93f0_dde97e994e83,adbeea58_9c39_11ed_93f0_dde97e994e83,adbeea59_9c39_11ed_93f0_dde97e994e83]
  Origin = -> Origin023
FEATURE [App::Part] CQ_assembly  label="Q6_CQ assembly_5b55deb75ded"
  Group = -> [adbeea56_9c39_11ed_93f0_dde97e994e83]
  Origin = -> Origin024
  Placement = pos=(65.45,-102.4,0) rot=(0,0,-1;1.5708rad)
FEATURE [Part::Feature] Part__Feature060  label="ECS-2520MV-480-BN-TR"
  shape: bbox 2.425 x 0.15 x 1.925 mm, 18 faces (baked)
FEATURE [Part::Feature] Part__Feature061  label="ECS-2520MV-480-BN-TR001"
  shape: bbox 2.3 x 0.05 x 1.8 mm, 10 faces (baked)
FEATURE [Part::Feature] Part__Feature062  label="ECS-2520MV-480-BN-TR002"
  shape: bbox 0.78 x 0.4 x 0.68 mm, 9 faces (baked)
FEATURE [Part::Feature] Part__Feature063  label="ECS-2520MV-480-BN-TR003"
  shape: bbox 0.78 x 0.4 x 0.68 mm, 10 faces (baked)
FEATURE [Part::Feature] Part__Feature064  label="ECS-2520MV-480-BN-TR004"
  shape: bbox 0.78 x 0.4 x 0.68 mm, 9 faces (baked)
FEATURE [Part::Feature] Part__Feature065  label="ECS-2520MV-480-BN-TR005"
  shape: bbox 0.78 x 0.4 x 0.68 mm, 9 faces (baked)
FEATURE [Part::Feature] Part__Feature066  label="ECS-2520MV-480-BN-TR006"
  shape: bbox 2.5 x 0.7 x 2 mm, 71 faces (baked)
FEATURE [Part::Feature] Part__Feature067  label="ECS-2520MV-480-BN-TR007"
  shape: bbox 0.5 x 0.4 x 0.1 mm, 10 faces (baked)
FEATURE [Part::Feature] Part__Feature068  label="ECS-2520MV-480-BN-TR008"
  shape: bbox 0.5 x 0.4 x 0.1 mm, 10 faces (baked)
FEATURE [App::Part] ECS_2520MV_480_BN_TR  label="Y1_ECS-2520MV-480-BN-TR009_a1ab40642b51"
  Group = -> [Part__Feature060,Part__Feature061,Part__Feature062,Part__Feature063,Part__Feature064,Part__Feature065,Part__Feature066,Part__Feature067,Part__Feature068]
  Origin = -> Origin025
  Placement = pos=(71.675,-27.725,0) rot=(0.57735,0.57735,0.57735;2.0944rad)
FEATURE [App::Link] R46_R_0603_1608Metric_774aaaae9ccb_ln_025  label="R68_R_0603_1608Metric_c1d0ac2a2113"
  LinkPlacement = pos=(95.875,-77.5,0) rot=(0,0,1;0rad)
  LinkedObject = -> Shape
  Placement = pos=(95.875,-77.5,0) rot=(0,0,1;0rad)
FEATURE [App::Link] R46_R_0603_1608Metric_774aaaae9ccb_ln_026  label="R49_R_0603_1608Metric_f08bca162405"
  LinkPlacement = pos=(41.4,-84.7,0) rot=(0,0,-1;1.5708rad)
  LinkedObject = -> Shape
  Placement = pos=(41.4,-84.7,0) rot=(0,0,-1;1.5708rad)
FEATURE [App::Link] Q6_CQ_assembly_5b55deb75ded_ln_  label="Q5_CQ assembly_13d97c03a934"
  LinkPlacement = pos=(54.4,-91.8,0) rot=(0,0,1;1.5708rad)
  LinkedObject = -> CQ_assembly
  Placement = pos=(54.4,-91.8,0) rot=(0,0,1;1.5708rad)
FEATURE [App::Link] R46_R_0603_1608Metric_774aaaae9ccb_ln_027  label="R16_R_0603_1608Metric_31f4b221a980"
  LinkPlacement = pos=(45.6,-24.475,0) rot=(0,0,-1;1.5708rad)
  LinkedObject = -> Shape
  Placement = pos=(45.6,-24.475,0) rot=(0,0,-1;1.5708rad)
FEATURE [App::Link] R46_R_0603_1608Metric_774aaaae9ccb_ln_028  label="R33_R_0603_1608Metric_3f1a9c301b58"
  LinkPlacement = pos=(55,-36.55,0) rot=(0,0,1;1.5708rad)
  LinkedObject = -> Shape
  Placement = pos=(55,-36.55,0) rot=(0,0,1;1.5708rad)
FEATURE [App::Link] R46_R_0603_1608Metric_774aaaae9ccb_ln_029  label="R19_R_0603_1608Metric_22b0ca13b083"
  LinkPlacement = pos=(44.675,-22.1,0) rot=(0,0,1;0rad)
  LinkedObject = -> Shape
  Placement = pos=(44.675,-22.1,0) rot=(0,0,1;0rad)
FEATURE [App::Link] C15_C_0603_1608Metric_07e9d6ced425_ln_013  label="C11_C_0603_1608Metric_dc6a99fc13d8"
  LinkPlacement = pos=(44.5,-33,0) rot=(0,0,1;0rad)
  LinkedObject = -> Shape002
  Placement = pos=(44.5,-33,0) rot=(0,0,1;0rad)
FEATURE [App::Link] C15_C_0603_1608Metric_07e9d6ced425_ln_014  label="C31_C_0603_1608Metric_91951cfdcf72"
  LinkPlacement = pos=(55.375,-50.2,0) rot=(0,0,1;3.14159rad)
  LinkedObject = -> Shape002
  Placement = pos=(55.375,-50.2,0) rot=(0,0,1;3.14159rad)
FEATURE [App::Link] R46_R_0603_1608Metric_774aaaae9ccb_ln_030  label="R48_R_0603_1608Metric_8ba37d3d64cb"
  LinkPlacement = pos=(39.5,-84.7,0) rot=(0,0,-1;1.5708rad)
  LinkedObject = -> Shape
  Placement = pos=(39.5,-84.7,0) rot=(0,0,-1;1.5708rad)
FEATURE [App::Link] R46_R_0603_1608Metric_774aaaae9ccb_ln_031  label="R4_R_0603_1608Metric_10eefd661c97"
  LinkPlacement = pos=(106.85,-104.875,0) rot=(0,0,1;3.14159rad)
  LinkedObject = -> Shape
  Placement = pos=(106.85,-104.875,0) rot=(0,0,1;3.14159rad)
FEATURE [App::Link] R46_R_0603_1608Metric_774aaaae9ccb_ln_032  label="R29_R_0603_1608Metric_6e6a0c4b09fb"
  LinkPlacement = pos=(71.1,-21.175,0) rot=(0,0,1;1.5708rad)
  LinkedObject = -> Shape
  Placement = pos=(71.1,-21.175,0) rot=(0,0,1;1.5708rad)
FEATURE [Part::Feature] Shape021  label="L10_L_TDK_SLF10145_814979705f2a"
  Placement = pos=(66.75,-52.8,0) rot=(0,0,1;3.14159rad)
  shape: bbox 10.61 x 10.61 x 4.5 mm, 72 faces (baked)
FEATURE [Part::Feature] Shape022  label="U11_SOT_353_SC_70_5_7dce9a71a436"
  Placement = pos=(85.4,-64,0) rot=(0,0,-1;1.5708rad)
  shape: bbox 2 x 2 x 1.05 mm, 104 faces (baked)
FEATURE [Part::Feature] Shape023  label="L9_SRU8028_f13f251f597f"
  Placement = pos=(42.6675,-63.45,0.05) rot=(1,0,0;1.5708rad)
  shape: bbox 8 x 8 x 2.8 mm, 37 faces (baked)
FEATURE [App::Link] C7_C_1210_3225Metric_ef0ee58cb2a3_ln_004  label="C33_C_1210_3225Metric_5171483d8a2a"
  LinkPlacement = pos=(48.25,-71.05,0) rot=(0,0,1;0rad)
  LinkedObject = -> Shape014
  Placement = pos=(48.25,-71.05,0) rot=(0,0,1;0rad)
FEATURE [App::Link] R46_R_0603_1608Metric_774aaaae9ccb_ln_033  label="R11_R_0603_1608Metric_ec7953592d81"
  LinkPlacement = pos=(107.75,-96.225,0) rot=(0,0,-1;1.5708rad)
  LinkedObject = -> Shape
  Placement = pos=(107.75,-96.225,0) rot=(0,0,-1;1.5708rad)
FEATURE [Part::Feature] Shape024  label="U5_HTSSOP_20_1EP_44x65mm_P065mm_EP34x65mm_Mask275x343mm_a4625a49efcb"
  Placement = pos=(53.45,-43.3625,0) rot=(0,0,1;1.5708rad)
  shape: bbox 6.5 x 6.72 x 1.6 mm, 341 faces (baked)
FEATURE [App::Link] R46_R_0603_1608Metric_774aaaae9ccb_ln_034  label="R69_R_0603_1608Metric_8b0235de1eda"
  LinkPlacement = pos=(118.2,-108.9,0) rot=(0,0,-1;1.5708rad)
  LinkedObject = -> Shape
  Placement = pos=(118.2,-108.9,0) rot=(0,0,-1;1.5708rad)
FEATURE [App::Link] R51_R_0805_2012Metric_3a37762b02a9_ln_  label="R50_R_0805_2012Metric_2430ad4fc0a6"
  LinkPlacement = pos=(52.9,-97.15,0) rot=(0,0,1;1.5708rad)
  LinkedObject = -> Shape011
  Placement = pos=(52.9,-97.15,0) rot=(0,0,1;1.5708rad)
FEATURE [App::Link] SW1_ASSEMBLY_b6ed21c688b7_ln_  label="SW2_ASSEMBLY_8f6bda97263c"
  LinkPlacement = pos=(110.8,-91.6,0) rot=(0,0,1;0rad)
  LinkedObject = -> ASSEMBLY
  Placement = pos=(110.8,-91.6,0) rot=(0,0,1;0rad)
FEATURE [App::Link] C15_C_0603_1608Metric_07e9d6ced425_ln_015  label="C16_C_0603_1608Metric_ee1b044c7939"
  LinkPlacement = pos=(58.7625,-33.375,0) rot=(0,0,1;1.5708rad)
  LinkedObject = -> Shape002
  Placement = pos=(58.7625,-33.375,0) rot=(0,0,1;1.5708rad)
FEATURE [App::Link] R46_R_0603_1608Metric_774aaaae9ccb_ln_035  label="R35_R_0603_1608Metric_69923e75e0c4"
  LinkPlacement = pos=(58.75,-36.525,0) rot=(0,0,1;1.5708rad)
  LinkedObject = -> Shape
  Placement = pos=(58.75,-36.525,0) rot=(0,0,1;1.5708rad)
FEATURE [Part::Feature] Part__Feature069  label="DX07S016JA1R1500"
  shape: bbox 0.25 x 0.06 x 2.431 mm, 6 faces (baked)
FEATURE [Part::Feature] Part__Feature070  label="DX07S016JA1R1501"
  shape: bbox 0.25 x 0.06 x 2.431 mm, 6 faces (baked)
FEATURE [Part::Feature] Part__Feature071  label="DX07S016JA1R1502"
  shape: bbox 0.25 x 0.06 x 1.831 mm, 10 faces (baked)
FEATURE [Part::Feature] Part__Feature072  label="DX07S016JA1R1503"
  shape: bbox 0.25 x 0.06 x 1.831 mm, 10 faces (baked)
FEATURE [Part::Feature] Part__Feature073  label="DX07S016JA1R1504"
  shape: bbox 0.25 x 0.06 x 2.431 mm, 6 faces (baked)
FEATURE [Part::Feature] Part__Feature074  label="DX07S016JA1R1505"
  shape: bbox 0.25 x 0.06 x 1.831 mm, 6 faces (baked)
FEATURE [Part::Feature] Part__Feature075  label="DX07S016JA1R1506"
  shape: bbox 0.25 x 0.06 x 1.831 mm, 10 faces (baked)
FEATURE [Part::Feature] Part__Feature076  label="DX07S016JA1R1507"
  shape: bbox 0.25 x 0.06 x 1.831 mm, 10 faces (baked)
FEATURE [Part::Feature] Part__Feature077  label="DX07S016JA1R1508"
  shape: bbox 0.25 x 0.06 x 1.831 mm, 6 faces (baked)
FEATURE [Part::Feature] Part__Feature078  label="DX07S016JA1R1509"
  shape: bbox 0.25 x 0.06 x 2.431 mm, 6 faces (baked)
FEATURE [Part::Feature] Part__Feature079  label="DX07S016JA1R1510"
  shape: bbox 0.25 x 0.06 x 1.831 mm, 10 faces (baked)
FEATURE [Part::Feature] Part__Feature080  label="DX07S016JA1R1511"
  shape: bbox 0.25 x 0.06 x 1.831 mm, 10 faces (baked)
FEATURE [Part::Feature] Part__Feature081  label="DX07S016JA1R1512"
  shape: bbox 0.25 x 0.06 x 2.431 mm, 6 faces (baked)
FEATURE [Part::Feature] Part__Feature082  label="DX07S016JA1R1513"
  shape: bbox 0.25 x 0.06 x 1.831 mm, 10 faces (baked)
FEATURE [Part::Feature] Part__Feature083  label="DX07S016JA1R1514"
  shape: bbox 0.25 x 0.06 x 1.831 mm, 10 faces (baked)
FEATURE [Part::Feature] Part__Feature084  label="DX07S016JA1R1515"
  shape: bbox 0.25 x 0.06 x 2.431 mm, 6 faces (baked)
FEATURE [Part::Feature] Part__Feature085  label="DX07S016JA1R1516"
  shape: bbox 0.25 x 0.06 x 1.831 mm, 6 faces (baked)
FEATURE [Part::Feature] Part__Feature086  label="DX07S016JA1R1517"
  shape: bbox 0.25 x 0.06 x 1.831 mm, 10 faces (baked)
FEATURE [Part::Feature] Part__Feature087  label="DX07S016JA1R1518"
  shape: bbox 0.25 x 0.06 x 1.831 mm, 10 faces (baked)
FEATURE [Part::Feature] Part__Feature088  label="DX07S016JA1R1519"
  shape: bbox 0.25 x 0.06 x 1.831 mm, 6 faces (baked)
FEATURE [Part::Feature] Part__Feature089  label="DX07S016JA1R1520"
  shape: bbox 0.25 x 0.06 x 2.431 mm, 6 faces (baked)
FEATURE [Part::Feature] Part__Feature090  label="DX07S016JA1R1521"
  shape: bbox 0.25 x 0.06 x 1.831 mm, 10 faces (baked)
FEATURE [Part::Feature] Part__Feature091  label="DX07S016JA1R1522"
  shape: bbox 0.25 x 0.06 x 1.831 mm, 10 faces (baked)
FEATURE [Part::Feature] Part__Feature092  label="DX07S016JA1R1523"
  shape: bbox 0.25 x 0.06 x 2.431 mm, 6 faces (baked)
FEATURE [Part::Feature] Part__Feature093  label="DX07S016JA1R1524"
  shape: bbox 8.94 x 4.36 x 6.9 mm, 446 faces (baked)
FEATURE [Part::Feature] Part__Feature094  label="DX07S016JA1R1525"
  shape: bbox 0.725 x 0.15 x 2.175 mm, 16 faces (baked)
FEATURE [Part::Feature] Part__Feature095  label="DX07S016JA1R1526"
  shape: bbox 0.725 x 0.15 x 2.175 mm, 15 faces (baked)
FEATURE [Part::Feature] Part__Feature096  label="DX07S016JA1R1527"
  shape: bbox 8.341 x 3.501 x 6.351 mm, 415 faces (baked)
FEATURE [Part::Feature] Part__Feature097  label="DX07S016JA1R1528"
  shape: bbox 0.2 x 0.43 x 0.625 mm, 10 faces (baked)
FEATURE [Part::Feature] Part__Feature098  label="DX07S016JA1R1529"
  shape: bbox 0.2 x 0.43 x 0.625 mm, 10 faces (baked)
FEATURE [Part::Feature] Part__Feature099  label="DX07S016JA1R1530"
  shape: bbox 0.2 x 0.43 x 0.625 mm, 10 faces (baked)
FEATURE [Part::Feature] Part__Feature100  label="DX07S016JA1R1531"
  shape: bbox 0.2 x 0.43 x 0.625 mm, 10 faces (baked)
FEATURE [Part::Feature] Part__Feature101  label="DX07S016JA1R1532"
  shape: bbox 0.2 x 0.43 x 0.625 mm, 10 faces (baked)
FEATURE [Part::Feature] Part__Feature102  label="DX07S016JA1R1533"
  shape: bbox 0.2 x 0.43 x 0.625 mm, 10 faces (baked)
FEATURE [Part::Feature] Part__Feature103  label="DX07S016JA1R1534"
  shape: bbox 0.2 x 0.43 x 0.625 mm, 10 faces (baked)
FEATURE [Part::Feature] Part__Feature104  label="DX07S016JA1R1535"
  shape: bbox 0.2 x 0.43 x 0.625 mm, 10 faces (baked)
FEATURE [Part::Feature] Part__Feature105  label="DX07S016JA1R1536"
  shape: bbox 0.2 x 0.43 x 0.625 mm, 10 faces (baked)
FEATURE [Part::Feature] Part__Feature106  label="DX07S016JA1R1537"
  shape: bbox 0.2 x 0.43 x 0.625 mm, 10 faces (baked)
FEATURE [Part::Feature] Part__Feature107  label="DX07S016JA1R1538"
  shape: bbox 0.2 x 0.43 x 0.625 mm, 10 faces (baked)
FEATURE [Part::Feature] Part__Feature108  label="DX07S016JA1R1539"
  shape: bbox 0.2 x 0.43 x 0.625 mm, 10 faces (baked)
FEATURE [Part::Feature] Part__Feature109  label="DX07S016JA1R1540"
  shape: bbox 0.2 x 0.43 x 0.625 mm, 10 faces (baked)
FEATURE [Part::Feature] Part__Feature110  label="DX07S016JA1R1541"
  shape: bbox 0.2 x 0.43 x 0.625 mm, 10 faces (baked)
FEATURE [Part::Feature] Part__Feature111  label="DX07S016JA1R1542"
  shape: bbox 0.2 x 0.43 x 0.625 mm, 10 faces (baked)
FEATURE [Part::Feature] Part__Feature112  label="DX07S016JA1R1543"
  shape: bbox 0.2 x 0.43 x 0.625 mm, 10 faces (baked)
FEATURE [App::Part] DX07S016JA1R1500  label="J3_DX07S016JA1R1544_f808be3fb0c2"
  Group = -> [Part__Feature069,Part__Feature070,Part__Feature071,Part__Feature072,Part__Feature073,Part__Feature074,Part__Feature075,Part__Feature076,Part__Feature077,Part__Feature078,Part__Feature079,Part__Feature080,Part__Feature081,Part__Feature082,Part__Feature083,Part__Feature084,Part__Feature085,Part__Feature086,Part__Feature087,Part__Feature088,Part__Feature089,Part__Feature090,Part__Feature091,+21 more]
  Origin = -> Origin026
  Placement = pos=(115.85,-101.125,0) rot=(0.57735,0.57735,0.57735;2.0944rad)
FEATURE [Part::Feature] Part__Feature113  label="ESP32-C6-WROOM-1U-N8-board"
  shape: bbox 0.85 x 0.8 x 0.9 mm, 10 faces (baked)
FEATURE [Part::Feature] Part__Feature114  label="ESP32-C6-WROOM-1U-N8-board001"
  shape: bbox 0.85 x 0.8 x 0.9 mm, 10 faces (baked)
FEATURE [Part::Feature] Part__Feature115  label="ESP32-C6-WROOM-1U-N8-board002"
  shape: bbox 0.85 x 0.8 x 0.9 mm, 10 faces (baked)
FEATURE [Part::Feature] Part__Feature116  label="ESP32-C6-WROOM-1U-N8-board003"
  shape: bbox 0.85 x 0.8 x 0.9 mm, 10 faces (baked)
FEATURE [Part::Feature] Part__Feature117  label="ESP32-C6-WROOM-1U-N8-board004"
  shape: bbox 0.85 x 0.8 x 0.9 mm, 10 faces (baked)
FEATURE [Part::Feature] Part__Feature118  label="ESP32-C6-WROOM-1U-N8-board005"
  shape: bbox 0.85 x 0.8 x 0.9 mm, 10 faces (baked)
FEATURE [Part::Feature] Part__Feature119  label="ESP32-C6-WROOM-1U-N8-board006"
  shape: bbox 0.85 x 0.8 x 0.9 mm, 10 faces (baked)
FEATURE [Part::Feature] Part__Feature120  label="ESP32-C6-WROOM-1U-N8-board007"
  shape: bbox 0.85 x 0.8 x 0.9 mm, 10 faces (baked)
FEATURE [Part::Feature] Part__Feature121  label="ESP32-C6-WROOM-1U-N8-board008"
  shape: bbox 0.85 x 0.8 x 0.9 mm, 10 faces (baked)
FEATURE [Part::Feature] Part__Feature122  label="ESP32-C6-WROOM-1U-N8-board009"
  shape: bbox 0.85 x 0.8 x 0.9 mm, 10 faces (baked)
FEATURE [Part::Feature] Part__Feature123  label="ESP32-C6-WROOM-1U-N8-board010"
  shape: bbox 0.85 x 0.8 x 0.9 mm, 10 faces (baked)
FEATURE [Part::Feature] Part__Feature124  label="ESP32-C6-WROOM-1U-N8-board011"
  shape: bbox 0.85 x 0.8 x 0.9 mm, 10 faces (baked)
FEATURE [Part::Feature] Part__Feature125  label="ESP32-C6-WROOM-1U-N8-board012"
  shape: bbox 0.85 x 0.8 x 0.9 mm, 10 faces (baked)
FEATURE [Part::Feature] Part__Feature126  label="ESP32-C6-WROOM-1U-N8-board013"
  shape: bbox 0.85 x 0.8 x 0.9 mm, 10 faces (baked)
FEATURE [Part::Feature] Part__Feature127  label="ESP32-C6-WROOM-1U-N8-board014"
  shape: bbox 0.85 x 0.8 x 0.9 mm, 10 faces (baked)
FEATURE [Part::Feature] Part__Feature128  label="ESP32-C6-WROOM-1U-N8-board015"
  shape: bbox 0.85 x 0.8 x 0.9 mm, 10 faces (baked)
FEATURE [Part::Feature] Part__Feature129  label="ESP32-C6-WROOM-1U-N8-board016"
  shape: bbox 0.85 x 0.8 x 0.9 mm, 10 faces (baked)
FEATURE [Part::Feature] Part__Feature130  label="ESP32-C6-WROOM-1U-N8-board017"
  shape: bbox 0.85 x 0.8 x 0.9 mm, 10 faces (baked)
FEATURE [Part::Feature] Part__Feature131  label="ESP32-C6-WROOM-1U-N8-board018"
  shape: bbox 0.85 x 0.8 x 0.9 mm, 10 faces (baked)
FEATURE [Part::Feature] Part__Feature132  label="ESP32-C6-WROOM-1U-N8-board019"
  shape: bbox 0.85 x 0.8 x 0.9 mm, 10 faces (baked)
FEATURE [Part::Feature] Part__Feature133  label="ESP32-C6-WROOM-1U-N8-board020"
  shape: bbox 0.85 x 0.8 x 0.9 mm, 10 faces (baked)
FEATURE [Part::Feature] Part__Feature134  label="ESP32-C6-WROOM-1U-N8-board021"
  shape: bbox 0.85 x 0.8 x 0.9 mm, 10 faces (baked)
FEATURE [Part::Feature] Part__Feature135  label="ESP32-C6-WROOM-1U-N8-board022"
  shape: bbox 0.85 x 0.8 x 0.9 mm, 10 faces (baked)
FEATURE [Part::Feature] Part__Feature136  label="ESP32-C6-WROOM-1U-N8-board023"
  shape: bbox 0.85 x 0.8 x 0.9 mm, 10 faces (baked)
FEATURE [Part::Feature] Part__Feature137  label="ESP32-C6-WROOM-1U-N8-board024"
  shape: bbox 0.85 x 0.8 x 0.9 mm, 10 faces (baked)
FEATURE [Part::Feature] Part__Feature138  label="ESP32-C6-WROOM-1U-N8-board025"
  shape: bbox 0.85 x 0.8 x 0.9 mm, 10 faces (baked)
FEATURE [Part::Feature] Part__Feature139  label="ESP32-C6-WROOM-1U-N8-board026"
  shape: bbox 0.85 x 0.8 x 0.9 mm, 10 faces (baked)
FEATURE [Part::Feature] Part__Feature140  label="ESP32-C6-WROOM-1U-N8-board027"
  shape: bbox 18 x 0.8 x 19.2 mm, 219 faces (baked)
FEATURE [Part::Feature] Part__Feature141  label="ESP32-C6-WROOM-1U-N8-board028"
  shape: bbox 0.85 x 0.8 x 0.9 mm, 10 faces (baked)
FEATURE [Part::Feature] Part__Feature142  label="ESP32-C6-WROOM-1U-N8-board029"
  shape: bbox 0.8 x 0.5 x 0.8 mm, 6 faces (baked)
FEATURE [Part::Feature] Part__Feature143  label="ESP32-C6-WROOM-1U-N8-board030"
  shape: bbox 0.8 x 0.5 x 0.8 mm, 6 faces (baked)
FEATURE [Part::Feature] Part__Feature144  label="ESP32-C6-WROOM-1U-N8-board031"
  shape: bbox 0.8 x 0.5 x 0.8 mm, 6 faces (baked)
FEATURE [Part::Feature] Part__Feature145  label="ESP32-C6-WROOM-1U-N8-board032"
  shape: bbox 0.8 x 0.5 x 0.8 mm, 6 faces (baked)
FEATURE [Part::Feature] Part__Feature146  label="ESP32-C6-WROOM-1U-N8-board033"
  shape: bbox 0.8 x 0.5 x 0.8 mm, 6 faces (baked)
FEATURE [Part::Feature] Part__Feature147  label="ESP32-C6-WROOM-1U-N8-board034"
  shape: bbox 0.8 x 0.5 x 0.8 mm, 6 faces (baked)
FEATURE [Part::Feature] Part__Feature148  label="ESP32-C6-WROOM-1U-N8-board035"
  shape: bbox 0.8 x 0.5 x 0.8 mm, 6 faces (baked)
FEATURE [Part::Feature] Part__Feature149  label="ESP32-C6-WROOM-1U-N8-board036"
  shape: bbox 0.8 x 0.5 x 0.8 mm, 6 faces (baked)
FEATURE [Part::Feature] Part__Feature150  label="ESP32-C6-WROOM-1U-N8-board037"
  shape: bbox 0.8 x 0.5 x 0.8 mm, 6 faces (baked)
FEATURE [Part::Feature] Part__Feature151  label="ESP32-C6-WROOM-1U-N8-board038"
  shape: bbox 15.65 x 2.452 x 17.5 mm, 57 faces (baked)
FEATURE [App::Part] ESP32_C6_WROOM_1U_N8_board  label="ESP32-C6-WROOM-1U-N8-board039"
  Group = -> [Part__Feature113,Part__Feature114,Part__Feature115,Part__Feature116,Part__Feature117,Part__Feature118,Part__Feature119,Part__Feature120,Part__Feature121,Part__Feature122,Part__Feature123,Part__Feature124,Part__Feature125,Part__Feature126,Part__Feature127,Part__Feature128,Part__Feature129,Part__Feature130,Part__Feature131,Part__Feature132,Part__Feature133,Part__Feature134,Part__Feature135,+16 more]
  Origin = -> Origin027
FEATURE [Part::Feature] Part__Feature152  label="antenna jack"
  Placement = pos=(6,0.8,-7.14) rot=(0,0,1;0rad)
  shape: bbox 1.8 x 0.16 x 0.5292 mm, 11 faces (baked)
FEATURE [Part::Feature] Part__Feature153  label="antenna jack001"
  Placement = pos=(6,0.8,-7.14) rot=(0,0,1;0rad)
  shape: bbox 2.051 x 1.501 x 0.8014 mm, 25 faces (baked)
FEATURE [Part::Feature] Part__Feature154  label="antenna jack002"
  Placement = pos=(6,0.8,-7.14) rot=(0,0,1;0rad)
  shape: bbox 2.6 x 0.45 x 2.6 mm, 53 faces (baked)
FEATURE [Part::Feature] Part__Feature155  label="antenna jack003"
  Placement = pos=(6,0.8,-7.14) rot=(0,0,1;0rad)
  shape: bbox 2.55 x 1.05 x 2 mm, 22 faces (baked)
FEATURE [Part::Feature] Part__Feature156  label="antenna jack004"
  Placement = pos=(6,0.8,-7.14) rot=(0,0,1;0rad)
  shape: bbox 1.8 x 0.16 x 0.5292 mm, 10 faces (baked)
FEATURE [App::Part] antenna_jack  label="antenna jack005"
  Group = -> [Part__Feature152,Part__Feature153,Part__Feature154,Part__Feature155,Part__Feature156]
  Origin = -> Origin028
FEATURE [App::Part] ESP32_C6_WROOM_1U_N8  label="U10_ESP32-C6-WROOM-1U-N8_f678ab5e8714"
  Group = -> [ESP32_C6_WROOM_1U_N8_board,antenna_jack]
  Origin = -> Origin029
  Placement = pos=(109.56,-79.455,0) rot=(0.57735,-0.57735,-0.57735;2.0944rad)
FEATURE [App::Link] C15_C_0603_1608Metric_07e9d6ced425_ln_016  label="C13_C_0603_1608Metric_510037309284"
  LinkPlacement = pos=(69.1,-27.725,0) rot=(0,0,1;1.5708rad)
  LinkedObject = -> Shape002
  Placement = pos=(69.1,-27.725,0) rot=(0,0,1;1.5708rad)
FEATURE [App::Link] C7_C_1210_3225Metric_ef0ee58cb2a3_ln_005  label="C32_C_1210_3225Metric_d559efe66f3d"
  LinkPlacement = pos=(42.95,-71.05,0) rot=(0,0,1;3.14159rad)
  LinkedObject = -> Shape014
  Placement = pos=(42.95,-71.05,0) rot=(0,0,1;3.14159rad)
FEATURE [App::Link] C7_C_1210_3225Metric_ef0ee58cb2a3_ln_006  label="C45_C_1210_3225Metric_68f334a9ffbc"
  LinkPlacement = pos=(74.2,-79.7,0) rot=(0,0,-1;1.5708rad)
  LinkedObject = -> Shape014
  Placement = pos=(74.2,-79.7,0) rot=(0,0,-1;1.5708rad)
FEATURE [Part::Feature] Shape025  label="J4_ARJP11A-MASA-B-A-EMU2_97b5dfc0d7ee"
  Placement = pos=(31.35,-31.05,0) rot=(0.57735,-0.57735,-0.57735;2.0944rad)
  shape: bbox 21.59 x 20.65 x 19.35 mm, 256 faces (baked)
FEATURE [Part::Feature] Part__Feature157  label="BxB-ZR-SM4_4"
  Placement = pos=(-6,4e-16,-1.85) rot=(0,1,0;3.14159rad)
  shape: bbox 9 x 5 x 3.7 mm, 62 faces (baked)
FEATURE [Part::Feature] Part__Feature158  label="BxB-ZR-SM4 pins_4"
  Placement = pos=(-6,4e-16,-1.85) rot=(0,1,0;3.14159rad)
  shape: bbox 0.6 x 3.75 x 2.5 mm, 16 faces (baked)
FEATURE [Part::Feature] Part__Feature159  label="BxB-ZR-SM4 pins_033"
  Placement = pos=(-6,4e-16,-1.85) rot=(0,1,0;3.14159rad)
  shape: bbox 0.5 x 0.5 x 1.5 mm, 6 faces (baked)
FEATURE [Part::Feature] Part__Feature160  label="BxB-ZR-SM4 pins_034"
  Placement = pos=(-6,4e-16,-1.85) rot=(0,1,0;3.14159rad)
  shape: bbox 0.5 x 2.4 x 0.5 mm, 6 faces (baked)
FEATURE [Part::Feature] Part__Feature161  label="BxB-ZR-SM4 pins_035"
  Placement = pos=(-6,4e-16,-1.85) rot=(0,1,0;3.14159rad)
  shape: bbox 0.6 x 3.75 x 2.5 mm, 16 faces (baked)
FEATURE [Part::Feature] Part__Feature162  label="BxB-ZR-SM4 pins_036"
  Placement = pos=(-6,4e-16,-1.85) rot=(0,1,0;3.14159rad)
  shape: bbox 0.5 x 0.5 x 1.5 mm, 6 faces (baked)
FEATURE [Part::Feature] Part__Feature163  label="BxB-ZR-SM4 pins_037"
  Placement = pos=(-6,4e-16,-1.85) rot=(0,1,0;3.14159rad)
  shape: bbox 0.5 x 2.4 x 0.5 mm, 6 faces (baked)
FEATURE [Part::Feature] Part__Feature164  label="BxB-ZR-SM4 pins_038"
  Placement = pos=(-6,4e-16,-1.85) rot=(0,1,0;3.14159rad)
  shape: bbox 0.5 x 0.5 x 1.5 mm, 6 faces (baked)
FEATURE [Part::Feature] Part__Feature165  label="BxB-ZR-SM4 pins_039"
  Placement = pos=(-6,4e-16,-1.85) rot=(0,1,0;3.14159rad)
  shape: bbox 0.5 x 2.4 x 0.5 mm, 6 faces (baked)
FEATURE [Part::Feature] Part__Feature166  label="BxB-ZR-SM4 pins_040"
  Placement = pos=(-6,4e-16,-1.85) rot=(0,1,0;3.14159rad)
  shape: bbox 0.5 x 0.5 x 1.5 mm, 6 faces (baked)
FEATURE [Part::Feature] Part__Feature167  label="BxB-ZR-SM4 pins_041"
  Placement = pos=(-6,4e-16,-1.85) rot=(0,1,0;3.14159rad)
  shape: bbox 0.5 x 2.4 x 0.5 mm, 6 faces (baked)
FEATURE [App::Part] BxB_ZR_SM4_pins_4  label="BxB-ZR-SM4 pins_042"
  Group = -> [Part__Feature158,Part__Feature159,Part__Feature160,Part__Feature161,Part__Feature162,Part__Feature163,Part__Feature164,Part__Feature165,Part__Feature166,Part__Feature167]
  Origin = -> Origin030
FEATURE [App::Part] B4B_ZR_SM4_TF  label="J8_B4B-ZR-SM4-TF_aa6069bc4ba5"
  Group = -> [Part__Feature157,BxB_ZR_SM4_pins_4]
  Origin = -> Origin031
  Placement = pos=(83,-113.9,0) rot=(0.57735,0.57735,0.57735;2.0944rad)
FEATURE [App::Link] R46_R_0603_1608Metric_774aaaae9ccb_ln_036  label="R15_R_0603_1608Metric_b1f3917b5047"
  LinkPlacement = pos=(47.1,-32.175,0) rot=(0,0,1;1.5708rad)
  LinkedObject = -> Shape
  Placement = pos=(47.1,-32.175,0) rot=(0,0,1;1.5708rad)
FEATURE [App::Link] C7_C_1210_3225Metric_ef0ee58cb2a3_ln_007  label="C47_C_1210_3225Metric_a793794abb8b"
  LinkPlacement = pos=(74.2,-84.9,0) rot=(0,0,1;1.5708rad)
  LinkedObject = -> Shape014
  Placement = pos=(74.2,-84.9,0) rot=(0,0,1;1.5708rad)
FEATURE [App::Link] C7_C_1210_3225Metric_ef0ee58cb2a3_ln_008  label="C52_C_1210_3225Metric_f27df306e403"
  LinkPlacement = pos=(88.2,-100.4,0) rot=(0,0,-1;1.5708rad)
  LinkedObject = -> Shape014
  Placement = pos=(88.2,-100.4,0) rot=(0,0,-1;1.5708rad)
FEATURE [Part::Feature] Part__Feature168  label="Relay_DPDT_Omron_G6K-2G"
  shape: bbox 6.6 x 10 x 5.8 mm, 107 faces (baked)
FEATURE [Part::Feature] Part__Feature169  label="Relay_DPDT_Omron_G6K-2G001"
  shape: bbox 4.5 x 8 x 0.15 mm, 6 faces (baked)
FEATURE [App::Part] Relay_DPDT_Omron_G6K_2G  label="K1_Relay_DPDT_Omron_G6K-2G002_613b893dd7d8"
  Group = -> [Part__Feature168,Part__Feature169]
  Origin = -> Origin032
  Placement = pos=(108.2,-113.9,0) rot=(0,0,1;0rad)
FEATURE [App::Link] C7_C_1210_3225Metric_ef0ee58cb2a3_ln_009  label="C28_C_1210_3225Metric_3f1c2ea51fa3"
  LinkPlacement = pos=(70.65,-65.025,0) rot=(0,0,-1;1.5708rad)
  LinkedObject = -> Shape014
  Placement = pos=(70.65,-65.025,0) rot=(0,0,-1;1.5708rad)
FEATURE [App::Link] D16_D_SOD_123_001db0ef50de_ln_001  label="D15_D_SOD_123_5ce035e10642"
  LinkPlacement = pos=(70.45,-98.85,0) rot=(0,0,1;1.5708rad)
  LinkedObject = -> Shape015
  Placement = pos=(70.45,-98.85,0) rot=(0,0,1;1.5708rad)
FEATURE [App::Link] R46_R_0603_1608Metric_774aaaae9ccb_ln_037  label="R40_R_0603_1608Metric_f7aa39ab128a"
  LinkPlacement = pos=(60.2,-56.775,0) rot=(0,0,-1;1.5708rad)
  LinkedObject = -> Shape
  Placement = pos=(60.2,-56.775,0) rot=(0,0,-1;1.5708rad)
FEATURE [App::Link] L4_L_0805_2012Metric_8a03def62cda_ln_002  label="L6_L_0805_2012Metric_48baee86d1bc"
  LinkPlacement = pos=(66.5375,-33.35,0) rot=(0,0,1;0rad)
  LinkedObject = -> Shape001
  Placement = pos=(66.5375,-33.35,0) rot=(0,0,1;0rad)
FEATURE [App::Link] C7_C_1210_3225Metric_ef0ee58cb2a3_ln_010  label="C9_C_1210_3225Metric_0b8fa2a5b136"
  LinkPlacement = pos=(70.775,-34.1,0) rot=(0,0,1;0rad)
  LinkedObject = -> Shape014
  Placement = pos=(70.775,-34.1,0) rot=(0,0,1;0rad)
FEATURE [App::Link] C15_C_0603_1608Metric_07e9d6ced425_ln_017  label="C19_C_0603_1608Metric_7cb6afb5b15e"
  LinkPlacement = pos=(62.5625,-33.375,0) rot=(0,0,1;1.5708rad)
  LinkedObject = -> Shape002
  Placement = pos=(62.5625,-33.375,0) rot=(0,0,1;1.5708rad)
FEATURE [App::Link] R46_R_0603_1608Metric_774aaaae9ccb_ln_038  label="R59_R_0603_1608Metric_56d724ab6627"
  LinkPlacement = pos=(76.425,-88.1,0) rot=(0,0,1;3.14159rad)
  LinkedObject = -> Shape
  Placement = pos=(76.425,-88.1,0) rot=(0,0,1;3.14159rad)
FEATURE [App::Link] R46_R_0603_1608Metric_774aaaae9ccb_ln_039  label="R66_R_0603_1608Metric_da4c424e134e"
  LinkPlacement = pos=(95.875,-81.5,0) rot=(0,0,1;0rad)
  LinkedObject = -> Shape
  Placement = pos=(95.875,-81.5,0) rot=(0,0,1;0rad)
FEATURE [Part::Feature] Part__Feature170  label="DQJ8"
  shape: bbox 5.75 x 1.1 x 4.9 mm, 100 faces (baked)
FEATURE [Part::Feature] Part__Feature171  label="DQJ009"
  shape: bbox 0.61 x 0.34 x 0.41 mm, 10 faces (baked)
FEATURE [Part::Feature] Part__Feature172  label="DQJ010"
  shape: bbox 4.29 x 0.34 x 4.9 mm, 50 faces (baked)
FEATURE [Part::Feature] Part__Feature173  label="DQJ011"
  shape: bbox 0.61 x 0.34 x 0.41 mm, 10 faces (baked)
FEATURE [Part::Feature] Part__Feature174  label="DQJ012"
  shape: bbox 0.61 x 0.34 x 0.41 mm, 10 faces (baked)
FEATURE [Part::Feature] Part__Feature175  label="DQJ013"
  shape: bbox 0.61 x 0.34 x 0.41 mm, 10 faces (baked)
FEATURE [App::Part] DQJ8  label="Q4_DQJ014_238d814497a5"
  Group = -> [Part__Feature170,Part__Feature171,Part__Feature172,Part__Feature173,Part__Feature174,Part__Feature175]
  Origin = -> Origin033
  Placement = pos=(64.5738,-91.8,0) rot=(1,0,0;1.5708rad)
FEATURE [Part::Feature] Part__Feature176  label="WDFN-8_511DH"
  shape: bbox 0.38 x 0.1 x 0.38 mm, 4 faces (baked)
FEATURE [Part::Feature] Part__Feature177  label="WDFN-8_511DH001"
  shape: bbox 3.3 x 0.75 x 3.3 mm, 53 faces (baked)
FEATURE [Part::Feature] Part__Feature178  label="WDFN-8_511DH002"
  shape: bbox 0.5 x 0.15 x 0.35 mm, 6 faces (baked)
FEATURE [Part::Feature] Part__Feature179  label="WDFN-8_511DH003"
  shape: bbox 2 x 0.15 x 2.3 mm, 30 faces (baked)
FEATURE [Part::Feature] Part__Feature180  label="WDFN-8_511DH004"
  shape: bbox 0.5 x 0.15 x 0.35 mm, 6 faces (baked)
FEATURE [Part::Feature] Part__Feature181  label="WDFN-8_511DH005"
  shape: bbox 0.5 x 0.15 x 0.35 mm, 6 faces (baked)
FEATURE [Part::Feature] Part__Feature182  label="WDFN-8_511DH006"
  shape: bbox 0.5 x 0.15 x 0.35 mm, 6 faces (baked)
FEATURE [App::Part] WDFN_8_511DH  label="Q2_WDFN-8_511DH007_0fe18143086f"
  Group = -> [Part__Feature176,Part__Feature177,Part__Feature178,Part__Feature179,Part__Feature180,Part__Feature181,Part__Feature182]
  Origin = -> Origin034
  Placement = pos=(61.1,-64.675,0) rot=(0.57735,-0.57735,-0.57735;2.0944rad)
FEATURE [App::Link] R46_R_0603_1608Metric_774aaaae9ccb_ln_040  label="R2_R_0603_1608Metric_d01ee5458398"
  LinkPlacement = pos=(110.45,-99.05,0) rot=(0,0,1;1.5708rad)
  LinkedObject = -> Shape
  Placement = pos=(110.45,-99.05,0) rot=(0,0,1;1.5708rad)
FEATURE [App::Link] C15_C_0603_1608Metric_07e9d6ced425_ln_018  label="C14_C_0603_1608Metric_54a9725b13dc"
  LinkPlacement = pos=(48.9,-32.125,0) rot=(0,0,1;1.5708rad)
  LinkedObject = -> Shape002
  Placement = pos=(48.9,-32.125,0) rot=(0,0,1;1.5708rad)
FEATURE [App::Link] R46_R_0603_1608Metric_774aaaae9ccb_ln_041  label="R32_R_0603_1608Metric_79e3abc5a02b"
  LinkPlacement = pos=(56.9,-36.55,0) rot=(0,0,-1;1.5708rad)
  LinkedObject = -> Shape
  Placement = pos=(56.9,-36.55,0) rot=(0,0,-1;1.5708rad)
FEATURE [Part::Feature] Shape026  label="R45_R_1206_3216Metric_2c348d52fadb"
  Placement = pos=(50.85,-59.675,0) rot=(0,0,1;0rad)
  shape: bbox 3.2 x 1.6 x 0.55 mm, 26 faces (baked)
FEATURE [App::Link] R46_R_0603_1608Metric_774aaaae9ccb_ln_042  label="R41_R_0603_1608Metric_08e8378e8507"
  LinkPlacement = pos=(52.025,-50.2,0) rot=(0,0,1;3.14159rad)
  LinkedObject = -> Shape
  Placement = pos=(52.025,-50.2,0) rot=(0,0,1;3.14159rad)
FEATURE [App::Link] R46_R_0603_1608Metric_774aaaae9ccb_ln_043  label="R28_R_0603_1608Metric_9f3453c6e36e"
  LinkPlacement = pos=(72.85,-21.175,0) rot=(0,0,-1;1.5708rad)
  LinkedObject = -> Shape
  Placement = pos=(72.85,-21.175,0) rot=(0,0,-1;1.5708rad)
FEATURE [Part::Feature] Shape027  label="U2_QFN-24-1EP_4x4mm_Pitch0.5mm_609023d98907"
  Placement = pos=(104.412,-101.325,0) rot=(0,0,1;0rad)
  shape: bbox 4 x 4 x 0.77 mm, 158 faces (baked)
FEATURE [App::Link] C15_C_0603_1608Metric_07e9d6ced425_ln_019  label="C21_C_0603_1608Metric_5171949a31c2"
  LinkPlacement = pos=(57.4,-20.9,0) rot=(0,0,-1;1.5708rad)
  LinkedObject = -> Shape002
  Placement = pos=(57.4,-20.9,0) rot=(0,0,-1;1.5708rad)
FEATURE [Part::Feature] Shape028  label="REF_128692_2018-10-31_827198fc0ad2"
  Placement = pos=(102.8,-51.4,6) rot=(0.57735,-0.57735,0.57735;4.18879rad)
  shape: bbox 41.21 x 41.21 x 12.57 mm, 2103 faces (baked)
FEATURE [App::Part] TopV_39ef
  Group = -> [Shape028]
  Origin = -> Origin006
FEATURE [App::Part] Step_Virtual_Models_39ef
  Group = -> [TopV_39ef]
  Origin = -> Origin005
FEATURE [App::Link] J8_B4B_ZR_SM4_TF_aa6069bc4ba5_ln_  label="J7_B4B-ZR-SM4-TF_32fb5e8bbcab"
  LinkPlacement = pos=(69,-41.55,0) rot=(0.57735,0.57735,0.57735;2.0944rad)
  LinkedObject = -> B4B_ZR_SM4_TF
  Placement = pos=(69,-41.55,0) rot=(0.57735,0.57735,0.57735;2.0944rad)
FEATURE [App::Link] R46_R_0603_1608Metric_774aaaae9ccb_ln_044  label="R47_R_0603_1608Metric_b1b00a594e16"
  LinkPlacement = pos=(55.325,-52,0) rot=(0,0,1;3.14159rad)
  LinkedObject = -> Shape
  Placement = pos=(55.325,-52,0) rot=(0,0,1;3.14159rad)
FEATURE [App::Link] R46_R_0603_1608Metric_774aaaae9ccb_ln_045  label="R42_R_0603_1608Metric_6d870ae6e2ad"
  LinkPlacement = pos=(49.4,-53.025,0) rot=(0,0,-1;1.5708rad)
  LinkedObject = -> Shape
  Placement = pos=(49.4,-53.025,0) rot=(0,0,-1;1.5708rad)
FEATURE [App::Link] J9_Molex_AE_6410_03A_8847f52549e1_ln_  label="J11_Molex_AE_6410_03A_a10ea7448a21"
  LinkPlacement = pos=(86.08,-69.18,0) rot=(0,0,1;3.14159rad)
  LinkedObject = -> Shape006
  Placement = pos=(86.08,-69.18,0) rot=(0,0,1;3.14159rad)
FEATURE [App::Link] R46_R_0603_1608Metric_774aaaae9ccb_ln_046  label="R31_R_0603_1608Metric_499632b2727e"
  LinkPlacement = pos=(69.925,-30,0) rot=(0,0,1;3.14159rad)
  LinkedObject = -> Shape
  Placement = pos=(69.925,-30,0) rot=(0,0,1;3.14159rad)
FEATURE [Part::Feature] Part__Feature183  label="FDS9945"
  shape: bbox 1.05 x 1.11 x 0.42 mm, 14 faces (baked)
FEATURE [Part::Feature] Part__Feature184  label="FDS9946"
  shape: bbox 1.05 x 1.11 x 0.42 mm, 14 faces (baked)
FEATURE [Part::Feature] Part__Feature185  label="FDS9947"
  shape: bbox 1.05 x 1.11 x 0.42 mm, 14 faces (baked)
FEATURE [Part::Feature] Part__Feature186  label="FDS9948"
  shape: bbox 1.05 x 1.11 x 0.42 mm, 14 faces (baked)
FEATURE [Part::Feature] Part__Feature187  label="FDS9949"
  shape: bbox 1.05 x 1.11 x 0.42 mm, 14 faces (baked)
FEATURE [Part::Feature] Part__Feature188  label="FDS9950"
  shape: bbox 1.05 x 1.11 x 0.42 mm, 14 faces (baked)
FEATURE [Part::Feature] Part__Feature189  label="FDS9951"
  shape: bbox 1.05 x 1.11 x 0.42 mm, 14 faces (baked)
FEATURE [Part::Feature] Part__Feature190  label="FDS9952"
  shape: bbox 1.05 x 1.11 x 0.42 mm, 14 faces (baked)
FEATURE [Part::Feature] Part__Feature191  label="FDS9953"
  shape: bbox 3.9 x 1.5 x 4.9 mm, 18 faces (baked)
FEATURE [Part::Feature] Part__Feature192  label="FDS9954"
  shape: bbox 0.5 x 0.1 x 0.5 mm, 4 faces (baked)
FEATURE [App::Part] FDS9945  label="Q3_FDS9955_ac763ffd1200"
  Group = -> [Part__Feature183,Part__Feature184,Part__Feature185,Part__Feature186,Part__Feature187,Part__Feature188,Part__Feature189,Part__Feature190,Part__Feature191,Part__Feature192]
  Origin = -> Origin035
  Placement = pos=(52.1,-64.575,0) rot=(1,0,0;1.5708rad)
FEATURE [App::Link] R46_R_0603_1608Metric_774aaaae9ccb_ln_047  label="R39_R_0603_1608Metric_53ff8c993f09"
  LinkPlacement = pos=(55.3,-55.6,0) rot=(0,0,1;3.14159rad)
  LinkedObject = -> Shape
  Placement = pos=(55.3,-55.6,0) rot=(0,0,1;3.14159rad)
FEATURE [App::Link] Q4_DQJ014_238d814497a5_ln_  label="Q7_DQJ014_88e23d041c6a"
  LinkPlacement = pos=(54.3975,-102.418,0) rot=(0,0.707107,0.707107;3.14159rad)
  LinkedObject = -> DQJ8
  Placement = pos=(54.3975,-102.418,0) rot=(0,0.707107,0.707107;3.14159rad)
FEATURE [Part::Feature] Shape029  label="U4_LQFP-48_7x7mm_P0.5mm_39a6bfeeede7"
  Placement = pos=(61.3625,-26.35,0) rot=(0,0,1;0rad)
  shape: bbox 9 x 9 x 1.5 mm, 747 faces (baked)
FEATURE [App::Link] R46_R_0603_1608Metric_774aaaae9ccb_ln_048  label="R30_R_0603_1608Metric_5431b640c5c4"
  LinkPlacement = pos=(69.35,-21.175,0) rot=(0,0,-1;1.5708rad)
  LinkedObject = -> Shape
  Placement = pos=(69.35,-21.175,0) rot=(0,0,-1;1.5708rad)
FEATURE [App::Link] R46_R_0603_1608Metric_774aaaae9ccb_ln_049  label="R36_R_0603_1608Metric_479c74451522"
  LinkPlacement = pos=(53.1,-36.55,0) rot=(0,0,1;1.5708rad)
  LinkedObject = -> Shape
  Placement = pos=(53.1,-36.55,0) rot=(0,0,1;1.5708rad)
FEATURE [App::Link] C7_C_1210_3225Metric_ef0ee58cb2a3_ln_011  label="C51_C_1210_3225Metric_8a1994725cf0"
  LinkPlacement = pos=(88.2,-79.8,0) rot=(0,0,1;1.5708rad)
  LinkedObject = -> Shape014
  Placement = pos=(88.2,-79.8,0) rot=(0,0,1;1.5708rad)
FEATURE [App::Link] R46_R_0603_1608Metric_774aaaae9ccb_ln_050  label="R10_R_0603_1608Metric_21e9adcacda2"
  LinkPlacement = pos=(102.05,-96.225,0) rot=(0,0,1;1.5708rad)
  LinkedObject = -> Shape
  Placement = pos=(102.05,-96.225,0) rot=(0,0,1;1.5708rad)
FEATURE [App::Link] R46_R_0603_1608Metric_774aaaae9ccb_ln_051  label="R55_R_0603_1608Metric_9fc18b426ef5"
  LinkPlacement = pos=(39.5,-91.5,0) rot=(0,0,-1;1.5708rad)
  LinkedObject = -> Shape
  Placement = pos=(39.5,-91.5,0) rot=(0,0,-1;1.5708rad)
FEATURE [App::Link] C15_C_0603_1608Metric_07e9d6ced425_ln_020  label="C12_C_0603_1608Metric_bff1b61a1585"
  LinkPlacement = pos=(44.475,-27.9,0) rot=(0,0,1;0rad)
  LinkedObject = -> Shape002
  Placement = pos=(44.475,-27.9,0) rot=(0,0,1;0rad)
FEATURE [App::Link] C7_C_1210_3225Metric_ef0ee58cb2a3_ln_012  label="C46_C_1210_3225Metric_5b2157100e13"
  LinkPlacement = pos=(74.2,-100.4,0) rot=(0,0,1;1.5708rad)
  LinkedObject = -> Shape014
  Placement = pos=(74.2,-100.4,0) rot=(0,0,1;1.5708rad)
FEATURE [App::Link] C15_C_0603_1608Metric_07e9d6ced425_ln_021  label="C48_C_0603_1608Metric_cb33312e204f"
  LinkPlacement = pos=(81.9,-99.9,0) rot=(0,0,-1;1.5708rad)
  LinkedObject = -> Shape002
  Placement = pos=(81.9,-99.9,0) rot=(0,0,-1;1.5708rad)
FEATURE [App::Link] R46_R_0603_1608Metric_774aaaae9ccb_ln_052  label="R63_R_0603_1608Metric_c9d91fc8ee54"
  LinkPlacement = pos=(113.5,-63.5,0) rot=(0,0,-1;1.5708rad)
  LinkedObject = -> Shape
  Placement = pos=(113.5,-63.5,0) rot=(0,0,-1;1.5708rad)
FEATURE [App::Link] C7_C_1210_3225Metric_ef0ee58cb2a3_ln_013  label="C50_C_1210_3225Metric_f7ae378cd339"
  LinkPlacement = pos=(88.2,-95.3,0) rot=(0,0,1;1.5708rad)
  LinkedObject = -> Shape014
  Placement = pos=(88.2,-95.3,0) rot=(0,0,1;1.5708rad)
FEATURE [App::Link] C34_C_1812_4532Metric_c9e1e99fbcf3_ln_  label="C35_C_1812_4532Metric_7ffa31b9f59f"
  LinkPlacement = pos=(48.55,-78.3,0) rot=(0,0,-1;1.5708rad)
  LinkedObject = -> Shape007
  Placement = pos=(48.55,-78.3,0) rot=(0,0,-1;1.5708rad)
FEATURE [App::Link] C42_CP_Elec_8x10_2bb510fd45c5_ln_  label="C43_CP_Elec_8x10_21484d6ba6d5"
  LinkPlacement = pos=(60.1,-112.392,0) rot=(0,0,-1;1.5708rad)
  LinkedObject = -> Shape008
  Placement = pos=(60.1,-112.392,0) rot=(0,0,-1;1.5708rad)
FEATURE [App::Link] R46_R_0603_1608Metric_774aaaae9ccb_ln_053  label="R65_R_0603_1608Metric_d096497a7c82"
  LinkPlacement = pos=(95.875,-83.3,0) rot=(0,0,1;0rad)
  LinkedObject = -> Shape
  Placement = pos=(95.875,-83.3,0) rot=(0,0,1;0rad)
FEATURE [App::Link] L4_L_0805_2012Metric_8a03def62cda_ln_003  label="L1_L_0805_2012Metric_ad938a6cd0fd"
  LinkPlacement = pos=(36.2,-107.4,0) rot=(0,0,-1;1.5708rad)
  LinkedObject = -> Shape001
  Placement = pos=(36.2,-107.4,0) rot=(0,0,-1;1.5708rad)
FEATURE [App::Link] J9_Molex_AE_6410_03A_8847f52549e1_ln_001  label="J10_Molex_AE_6410_03A_c93265be13e0"
  LinkPlacement = pos=(116.3,-117.7,0) rot=(0,0,1;1.5708rad)
  LinkedObject = -> Shape006
  Placement = pos=(116.3,-117.7,0) rot=(0,0,1;1.5708rad)
FEATURE [App::Link] Q8_SC_59_2bd4244db7e1_ln_005  label="D8_SC_59_36c6ebe37a8e"
  LinkPlacement = pos=(66.35,-65.425,0) rot=(0,0,1;1.5708rad)
  LinkedObject = -> Shape009
  Placement = pos=(66.35,-65.425,0) rot=(0,0,1;1.5708rad)
FEATURE [App::Link] L4_L_0805_2012Metric_8a03def62cda_ln_004  label="L3_L_0805_2012Metric_6e33afbc1ae0"
  LinkPlacement = pos=(36.31,-43.75,0) rot=(0,0,-1;1.5708rad)
  LinkedObject = -> Shape001
  Placement = pos=(36.31,-43.75,0) rot=(0,0,-1;1.5708rad)
FEATURE [App::Part] Top_39ef
  Group = -> [Shape,R46_R_0603_1608Metric_774aaaae9ccb_ln_,Shape001,Shape002,R46_R_0603_1608Metric_774aaaae9ccb_ln_001,Shape003,C15_C_0603_1608Metric_07e9d6ced425_ln_,Shape004,DR74_2R2_R,R46_R_0603_1608Metric_774aaaae9ccb_ln_002,R46_R_0603_1608Metric_774aaaae9ccb_ln_003,Shape005,B6B_ZR_SM4_TF,Shape006,R46_R_0603_1608Metric_774aaaae9ccb_ln_004,part,Shape007,R46_R_0603_1608Metric_774aaaae9ccb_ln_005,+149 more]
  Origin = -> Origin003
FEATURE [Part::Feature] Shape030  label="U3_SOT_23_5_fbfa03686d3a"
  Placement = pos=(38.7375,-22.1,-1.6) rot=(1,0,0;3.14159rad)
  shape: bbox 2.8 x 2.9 x 1.55 mm, 109 faces (baked)
FEATURE [App::Link] C15_C_0603_1608Metric_07e9d6ced425_ln_022  label="C56_C_0603_1608Metric_175341d4f240"
  LinkPlacement = pos=(98.525,-69.1,-1.6) rot=(0,1,0;3.14159rad)
  LinkedObject = -> Shape002
  Placement = pos=(98.525,-69.1,-1.6) rot=(0,1,0;3.14159rad)
FEATURE [App::Link] R46_R_0603_1608Metric_774aaaae9ccb_ln_054  label="R5_R_0603_1608Metric_193897be06f0"
  LinkPlacement = pos=(102.925,-100.375,-1.6) rot=(0,1,0;3.14159rad)
  LinkedObject = -> Shape
  Placement = pos=(102.925,-100.375,-1.6) rot=(0,1,0;3.14159rad)
FEATURE [App::Link] R46_R_0603_1608Metric_774aaaae9ccb_ln_055  label="R27_R_0603_1608Metric_984ac03a0c6b"
  LinkPlacement = pos=(113.5,-63.5,-1.6) rot=(0.707107,-0.707107,0;3.14159rad)
  LinkedObject = -> Shape
  Placement = pos=(113.5,-63.5,-1.6) rot=(0.707107,-0.707107,0;3.14159rad)
FEATURE [App::Link] R46_R_0603_1608Metric_774aaaae9ccb_ln_056  label="R26_R_0603_1608Metric_cfc28ab9c151"
  LinkPlacement = pos=(111.6,-63.5,-1.6) rot=(0.707107,-0.707107,0;3.14159rad)
  LinkedObject = -> Shape
  Placement = pos=(111.6,-63.5,-1.6) rot=(0.707107,-0.707107,0;3.14159rad)
FEATURE [App::Link] C7_C_1210_3225Metric_ef0ee58cb2a3_ln_014  label="C57_C_1210_3225Metric_4b7ee702d23f"
  LinkPlacement = pos=(107.8,-75.9,-1.6) rot=(1,0,0;3.14159rad)
  LinkedObject = -> Shape014
  Placement = pos=(107.8,-75.9,-1.6) rot=(1,0,0;3.14159rad)
FEATURE [App::Link] L4_L_0805_2012Metric_8a03def62cda_ln_005  label="L14_L_0805_2012Metric_4cf34794a886"
  LinkPlacement = pos=(107.8,-73,-1.6) rot=(1,0,0;3.14159rad)
  LinkedObject = -> Shape001
  Placement = pos=(107.8,-73,-1.6) rot=(1,0,0;3.14159rad)
FEATURE [App::Link] R46_R_0603_1608Metric_774aaaae9ccb_ln_057  label="R24_R_0603_1608Metric_19c57862a23c"
  LinkPlacement = pos=(105.9,-63.5,-1.6) rot=(0.707107,-0.707107,0;3.14159rad)
  LinkedObject = -> Shape
  Placement = pos=(105.9,-63.5,-1.6) rot=(0.707107,-0.707107,0;3.14159rad)
FEATURE [App::Link] C15_C_0603_1608Metric_07e9d6ced425_ln_023  label="C2_C_0603_1608Metric_94fea23fcdd7"
  LinkPlacement = pos=(31.735,-53.25,-1.6) rot=(0,1,0;3.14159rad)
  LinkedObject = -> Shape002
  Placement = pos=(31.735,-53.25,-1.6) rot=(0,1,0;3.14159rad)
FEATURE [App::Link] C25_C_0805_2012Metric_74a1367a9602_ln_002  label="C6_C_0805_2012Metric_2a4f8ed82148"
  LinkPlacement = pos=(103.65,-104.875,-1.6) rot=(0,1,0;3.14159rad)
  LinkedObject = -> Shape010
  Placement = pos=(103.65,-104.875,-1.6) rot=(0,1,0;3.14159rad)
FEATURE [App::Link] R46_R_0603_1608Metric_774aaaae9ccb_ln_058  label="R23_R_0603_1608Metric_28cd30abe862"
  LinkPlacement = pos=(104,-63.5,-1.6) rot=(0.707107,-0.707107,0;3.14159rad)
  LinkedObject = -> Shape
  Placement = pos=(104,-63.5,-1.6) rot=(0.707107,-0.707107,0;3.14159rad)
FEATURE [App::Link] C25_C_0805_2012Metric_74a1367a9602_ln_003  label="C54_C_0805_2012Metric_6d5c90f87a38"
  LinkPlacement = pos=(115.4,-63.5,-1.6) rot=(0.707107,0.707107,0;3.14159rad)
  LinkedObject = -> Shape010
  Placement = pos=(115.4,-63.5,-1.6) rot=(0.707107,0.707107,0;3.14159rad)
FEATURE [App::Link] C15_C_0603_1608Metric_07e9d6ced425_ln_024  label="C1_C_0603_1608Metric_33a120b9dfd3"
  LinkPlacement = pos=(31.625,-116.9,-1.6) rot=(0,1,0;3.14159rad)
  LinkedObject = -> Shape002
  Placement = pos=(31.625,-116.9,-1.6) rot=(0,1,0;3.14159rad)
FEATURE [App::Link] C15_C_0603_1608Metric_07e9d6ced425_ln_025  label="C58_C_0603_1608Metric_dcb1786011ea"
  LinkPlacement = pos=(115.925,-73,-1.6) rot=(0,1,0;3.14159rad)
  LinkedObject = -> Shape002
  Placement = pos=(115.925,-73,-1.6) rot=(0,1,0;3.14159rad)
FEATURE [App::Link] C25_C_0805_2012Metric_74a1367a9602_ln_004  label="C18_C_0805_2012Metric_b203f93a33c0"
  LinkPlacement = pos=(60.3625,-26.45,-1.6) rot=(0,1,0;3.14159rad)
  LinkedObject = -> Shape010
  Placement = pos=(60.3625,-26.45,-1.6) rot=(0,1,0;3.14159rad)
FEATURE [App::Link] C25_C_0805_2012Metric_74a1367a9602_ln_005  label="C55_C_0805_2012Metric_d5ca0dbbabba"
  LinkPlacement = pos=(107.8,-63.5,-1.6) rot=(0.707107,0.707107,0;3.14159rad)
  LinkedObject = -> Shape010
  Placement = pos=(107.8,-63.5,-1.6) rot=(0.707107,0.707107,0;3.14159rad)
FEATURE [App::Link] R46_R_0603_1608Metric_774aaaae9ccb_ln_059  label="R1_R_0603_1608Metric_8d31debdda68"
  LinkPlacement = pos=(27.4,-31.15,-1.6) rot=(0.707107,0.707107,0;3.14159rad)
  LinkedObject = -> Shape
  Placement = pos=(27.4,-31.15,-1.6) rot=(0.707107,0.707107,0;3.14159rad)
FEATURE [App::Link] C15_C_0603_1608Metric_07e9d6ced425_ln_026  label="C20_C_0603_1608Metric_c069164ce9b9"
  LinkPlacement = pos=(63.1125,-27.6,-1.6) rot=(0.707107,0.707107,0;3.14159rad)
  LinkedObject = -> Shape002
  Placement = pos=(63.1125,-27.6,-1.6) rot=(0.707107,0.707107,0;3.14159rad)
FEATURE [App::Link] R46_R_0603_1608Metric_774aaaae9ccb_ln_060  label="R6_R_0603_1608Metric_d0082f3021ca"
  LinkPlacement = pos=(102.975,-102.375,-1.6) rot=(0,1,0;3.14159rad)
  LinkedObject = -> Shape
  Placement = pos=(102.975,-102.375,-1.6) rot=(0,1,0;3.14159rad)
FEATURE [App::Link] U8_SOT_23_6_8216086f4dbc_ln_001  label="U1_SOT_23_6_1e4507a77672"
  LinkPlacement = pos=(106.85,-101.375,-1.6) rot=(0,1,0;3.14159rad)
  LinkedObject = -> Shape005
  Placement = pos=(106.85,-101.375,-1.6) rot=(0,1,0;3.14159rad)
FEATURE [App::Link] R46_R_0603_1608Metric_774aaaae9ccb_ln_061  label="R8_R_0603_1608Metric_95b27f307396"
  LinkPlacement = pos=(106.85,-104.875,-1.6) rot=(0,1,0;3.14159rad)
  LinkedObject = -> Shape
  Placement = pos=(106.85,-104.875,-1.6) rot=(0,1,0;3.14159rad)
FEATURE [App::Link] R46_R_0603_1608Metric_774aaaae9ccb_ln_062  label="R25_R_0603_1608Metric_81cbe49e2c89"
  LinkPlacement = pos=(109.7,-63.5,-1.6) rot=(0.707107,-0.707107,0;3.14159rad)
  LinkedObject = -> Shape
  Placement = pos=(109.7,-63.5,-1.6) rot=(0.707107,-0.707107,0;3.14159rad)
FEATURE [App::Link] C34_C_1812_4532Metric_c9e1e99fbcf3_ln_001  label="C3_C_1812_4532Metric_cae62f728013"
  LinkPlacement = pos=(31.4,-31.2,-1.6) rot=(0.707107,0.707107,0;3.14159rad)
  LinkedObject = -> Shape007
  Placement = pos=(31.4,-31.2,-1.6) rot=(0.707107,0.707107,0;3.14159rad)
FEATURE [App::Link] R46_R_0603_1608Metric_774aaaae9ccb_ln_063  label="R18_R_0603_1608Metric_75aac378467d"
  LinkPlacement = pos=(60.3625,-28.35,-1.6) rot=(0,1,0;3.14159rad)
  LinkedObject = -> Shape
  Placement = pos=(60.3625,-28.35,-1.6) rot=(0,1,0;3.14159rad)
FEATURE [App::Link] R46_R_0603_1608Metric_774aaaae9ccb_ln_064  label="R22_R_0603_1608Metric_0303f93a7074"
  LinkPlacement = pos=(102.1,-63.5,-1.6) rot=(0.707107,-0.707107,0;3.14159rad)
  LinkedObject = -> Shape
  Placement = pos=(102.1,-63.5,-1.6) rot=(0.707107,-0.707107,0;3.14159rad)
FEATURE [App::Link] R46_R_0603_1608Metric_774aaaae9ccb_ln_065  label="R62_R_0603_1608Metric_e462ee4acfc1"
  LinkPlacement = pos=(98.525,-67.2,-1.6) rot=(1,0,0;3.14159rad)
  LinkedObject = -> Shape
  Placement = pos=(98.525,-67.2,-1.6) rot=(1,0,0;3.14159rad)
FEATURE [App::Part] Bot_39ef
  Group = -> [Shape030,C15_C_0603_1608Metric_07e9d6ced425_ln_022,R46_R_0603_1608Metric_774aaaae9ccb_ln_054,R46_R_0603_1608Metric_774aaaae9ccb_ln_055,R46_R_0603_1608Metric_774aaaae9ccb_ln_056,C7_C_1210_3225Metric_ef0ee58cb2a3_ln_014,L4_L_0805_2012Metric_8a03def62cda_ln_005,R46_R_0603_1608Metric_774aaaae9ccb_ln_057,C15_C_0603_1608Metric_07e9d6ced425_ln_023,C25_C_0805_2012Metric_74a1367a9602_ln_002,+16 more]
  Origin = -> Origin004
FEATURE [App::Part] Step_Models_39ef
  Group = -> [Top_39ef,Bot_39ef]
  Origin = -> Origin002
FEATURE [App::Part] Board_39ef  label="mpair"
  Group = -> [Local_CS_39ef,Board_Geoms_39ef,Step_Models_39ef,Step_Virtual_Models_39ef]
  Origin = -> Origin001
